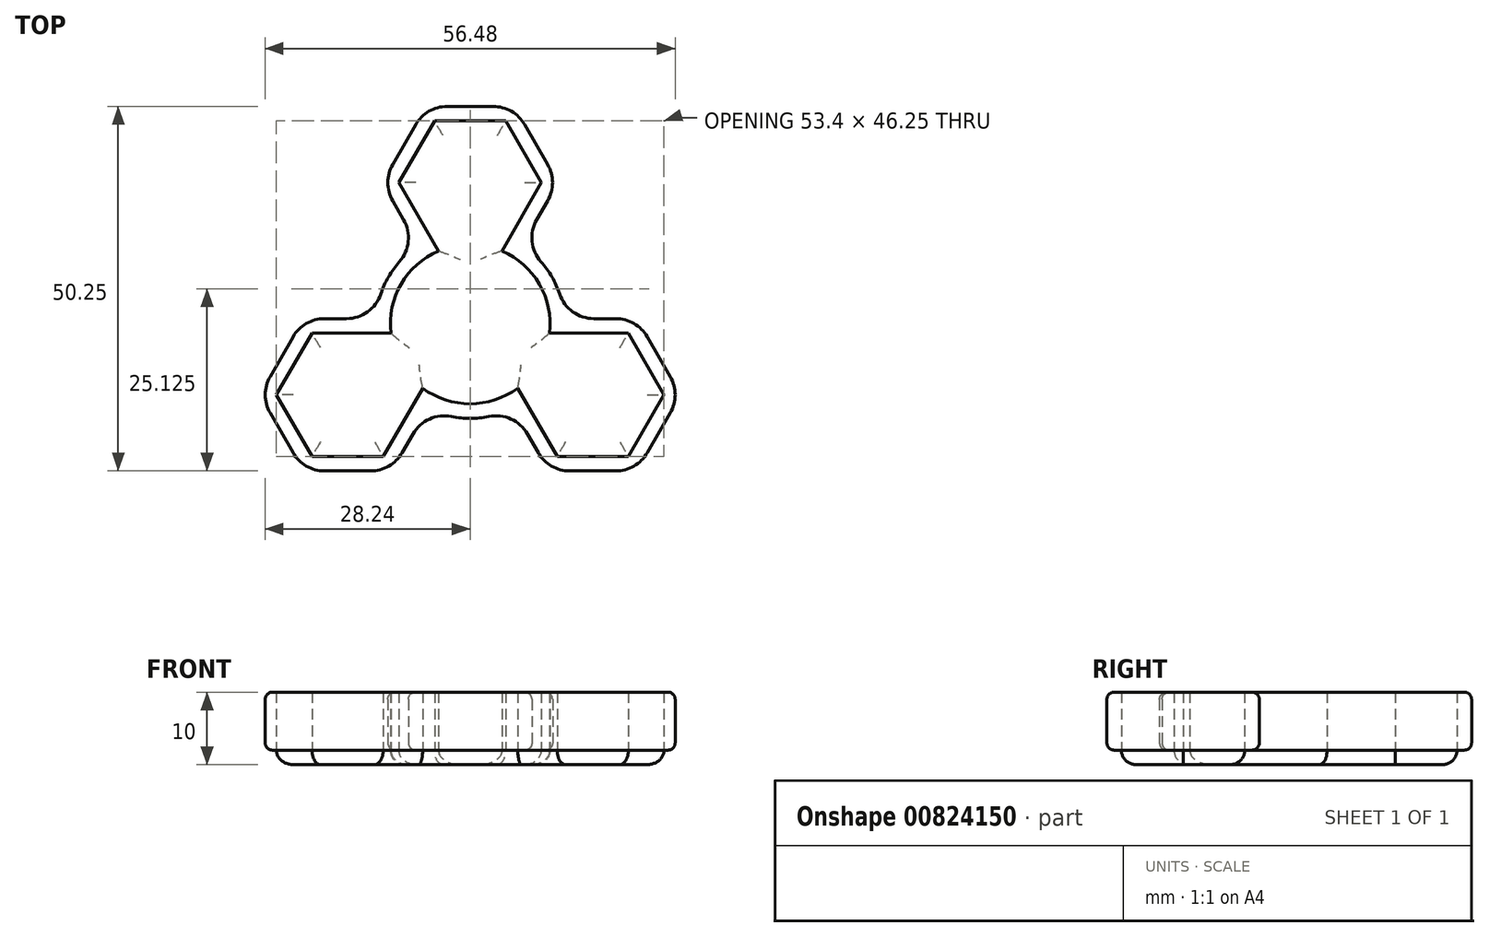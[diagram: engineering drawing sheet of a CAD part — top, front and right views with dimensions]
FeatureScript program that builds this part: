
annotation { "Feature Type Name" : "Feature", "Feature Type Description" : "" }
export const myFeature = defineFeature(function(context is Context, id is Id, definition is map)
    precondition{}
    {
        {
            var Q0;
            Q0=qCreatedBy(makeId("Top.planeOp"),FACE);
            var sketch = newSketch(context, id + "F0", { "sketchPlane" : qUnion([Q0])});
            skCircle(sketch, "E0", {"center": v(0, 0) * mm, "radius": 11 * mm, "construction": true});
            skCircle(sketch, "E1", {"center": v(0, 19.5) * mm, "radius": 8.5 * mm, "construction": true});
            skLineSegment(sketch, "E2", {"start": v(0, 19.5) * mm, "end": v(0, 0) * mm, "construction": true});
            skLineSegment(sketch, "E3", {"start": v(-4.9, 28) * mm, "end": v(4.9, 28) * mm});
            skLineSegment(sketch, "E4", {"start": v(-4.9, 28) * mm, "end": v(-9.81, 19.5) * mm});
            skLineSegment(sketch, "E5", {"start": v(-9.81, 19.5) * mm, "end": v(-4.9, 11) * mm});
            skLineSegment(sketch, "E6", {"start": v(-4.9, 11) * mm, "end": v(4.9, 11) * mm, "construction": true});
            skLineSegment(sketch, "E7", {"start": v(4.9, 11) * mm, "end": v(9.81, 19.5) * mm});
            skLineSegment(sketch, "E8", {"start": v(9.81, 19.5) * mm, "end": v(4.9, 28) * mm});
            skCircle(sketch, "E9", {"center": v(16.89, -9.75) * mm, "radius": 8.5 * mm, "construction": true});
            skLineSegment(sketch, "E10", {"start": v(11.98, -1.25) * mm, "end": v(21.8, -1.25) * mm});
            skLineSegment(sketch, "E11", {"start": v(11.98, -1.25) * mm, "end": v(7.07, -9.75) * mm, "construction": true});
            skLineSegment(sketch, "E12", {"start": v(7.07, -9.75) * mm, "end": v(11.98, -18.25) * mm});
            skLineSegment(sketch, "E13", {"start": v(11.98, -18.25) * mm, "end": v(21.8, -18.25) * mm});
            skLineSegment(sketch, "E14", {"start": v(21.8, -18.25) * mm, "end": v(26.7, -9.75) * mm});
            skLineSegment(sketch, "E15", {"start": v(26.7, -9.75) * mm, "end": v(21.8, -1.25) * mm});
            skLineSegment(sketch, "E16", {"start": v(0, 0) * mm, "end": v(16.89, -9.75) * mm, "construction": true});
            skCircle(sketch, "E17", {"center": v(-16.89, -9.75) * mm, "radius": 8.5 * mm, "construction": true});
            skLineSegment(sketch, "E18", {"start": v(-21.8, -1.25) * mm, "end": v(-11.98, -1.25) * mm});
            skLineSegment(sketch, "E19", {"start": v(-21.8, -1.25) * mm, "end": v(-26.7, -9.75) * mm});
            skLineSegment(sketch, "E20", {"start": v(-26.7, -9.75) * mm, "end": v(-21.8, -18.25) * mm});
            skLineSegment(sketch, "E21", {"start": v(-21.8, -18.25) * mm, "end": v(-11.98, -18.25) * mm});
            skLineSegment(sketch, "E22", {"start": v(-11.98, -18.25) * mm, "end": v(-7.07, -9.75) * mm});
            skLineSegment(sketch, "E23", {"start": v(-7.07, -9.75) * mm, "end": v(-11.98, -1.25) * mm, "construction": true});
            skLineSegment(sketch, "E24", {"start": v(-16.89, -9.75) * mm, "end": v(0, 0) * mm, "construction": true});
            skLineSegment(sketch, "E25", {"start": v(-4.9, 11) * mm, "end": v(-4.38, 10.09) * mm});
            skLineSegment(sketch, "E26", {"start": v(4.9, 11) * mm, "end": v(4.38, 10.09) * mm});
            skLineSegment(sketch, "E27", {"start": v(-11.98, -1.25) * mm, "end": v(-10.93, -1.25) * mm});
            skLineSegment(sketch, "E28", {"start": v(-7.07, -9.75) * mm, "end": v(-6.55, -8.84) * mm});
            skLineSegment(sketch, "E29", {"start": v(7.07, -9.75) * mm, "end": v(6.55, -8.84) * mm});
            skLineSegment(sketch, "E30", {"start": v(11.98, -1.25) * mm, "end": v(10.93, -1.25) * mm});
            skArc(sketch, "E31", {"start": v(-4.38, 10.09) * mm, "mid": v(-9.53, 5.5) * mm, "end": v(-10.93, -1.25) * mm});
            skArc(sketch, "E32", {"start": v(4.38, 10.09) * mm, "mid": v(9.53, 5.5) * mm, "end": v(10.93, -1.25) * mm});
            skArc(sketch, "E33", {"start": v(-6.55, -8.84) * mm, "mid": v(0, -11) * mm, "end": v(6.55, -8.84) * mm});
            skLineSegment(sketch, "E34.0", {"start": v(-6.06, 30) * mm, "end": v(-12.12, 19.5) * mm});
            skLineSegment(sketch, "E34.1", {"start": v(-6.06, 30) * mm, "end": v(6.06, 30) * mm});
            skLineSegment(sketch, "E34.2", {"start": v(12.12, 19.5) * mm, "end": v(6.06, 30) * mm});
            skLineSegment(sketch, "E34.3", {"start": v(7.14, 10.86) * mm, "end": v(12.12, 19.5) * mm});
            skArc(sketch, "E34.4", {"start": v(7.14, 10.86) * mm, "mid": v(11.26, 6.5) * mm, "end": v(12.98, 0.75) * mm});
            skLineSegment(sketch, "E34.5", {"start": v(-12.12, 19.5) * mm, "end": v(-7.14, 10.86) * mm});
            skLineSegment(sketch, "E34.6", {"start": v(12.98, 0.75) * mm, "end": v(22.95, 0.75) * mm});
            skLineSegment(sketch, "E34.7", {"start": v(29.01, -9.75) * mm, "end": v(22.95, 0.75) * mm});
            skLineSegment(sketch, "E34.8", {"start": v(-29.01, -9.75) * mm, "end": v(-22.95, -20.25) * mm});
            skLineSegment(sketch, "E34.9", {"start": v(-22.95, 0.75) * mm, "end": v(-29.01, -9.75) * mm});
            skLineSegment(sketch, "E34.10", {"start": v(-22.95, 0.75) * mm, "end": v(-12.98, 0.75) * mm});
            skArc(sketch, "E34.11", {"start": v(-7.14, 10.86) * mm, "mid": v(-11.26, 6.5) * mm, "end": v(-12.98, 0.75) * mm});
            skLineSegment(sketch, "E34.12", {"start": v(-22.95, -20.25) * mm, "end": v(-10.83, -20.25) * mm});
            skLineSegment(sketch, "E34.13", {"start": v(-10.83, -20.25) * mm, "end": v(-5.84, -11.61) * mm});
            skArc(sketch, "E34.14", {"start": v(-5.84, -11.61) * mm, "mid": v(0, -13) * mm, "end": v(5.84, -11.61) * mm});
            skLineSegment(sketch, "E34.15", {"start": v(5.84, -11.61) * mm, "end": v(10.83, -20.25) * mm});
            skLineSegment(sketch, "E34.16", {"start": v(10.83, -20.25) * mm, "end": v(22.95, -20.25) * mm});
            skLineSegment(sketch, "E34.17", {"start": v(22.95, -20.25) * mm, "end": v(29.01, -9.75) * mm});
            skSolve(sketch);
        }
        {
            var Q0;
            Q0=makeQuery(id+"F0.imprint","IMPRINT",FACE,{"disambiguationData":[TD([[makeQuery(id+"F0.imprint","IMPRINT",EDGE,{"derivedFrom":sQuery(id+"F0.wireOp",EDGE,"E3")}),1.0]])]});
            extrude(context, id + "F1", {"entities" : qUnion([Q0]), "depth" : 8 * mm, "offsetDistance" : 25 * mm});
        }
        {
            var Q0;
            Q0=makeQuery(id+"F1.opExtrude","SWEPT_EDGE",EDGE,{"disambiguationData":[OSD([sQuery(id+"F0.wireOp",EDGE,"E34.4"),sQuery(id+"F0.wireOp",EDGE,"E34.6")])]});
            var Q1;
            Q1=makeQuery(id+"F1.opExtrude","SWEPT_EDGE",EDGE,{"disambiguationData":[OSD([sQuery(id+"F0.wireOp",EDGE,"E34.3"),sQuery(id+"F0.wireOp",EDGE,"E34.4")])]});
            var Q2;
            Q2=makeQuery(id+"F1.opExtrude","SWEPT_EDGE",EDGE,{"disambiguationData":[OSD([sQuery(id+"F0.wireOp",EDGE,"E34.14"),sQuery(id+"F0.wireOp",EDGE,"E34.15")])]});
            var Q3;
            Q3=makeQuery(id+"F1.opExtrude","SWEPT_EDGE",EDGE,{"disambiguationData":[OSD([sQuery(id+"F0.wireOp",EDGE,"E34.13"),sQuery(id+"F0.wireOp",EDGE,"E34.14")])]});
            var Q4;
            Q4=makeQuery(id+"F1.opExtrude","SWEPT_EDGE",EDGE,{"disambiguationData":[OSD([sQuery(id+"F0.wireOp",EDGE,"E34.10"),sQuery(id+"F0.wireOp",EDGE,"E34.11")])]});
            var Q5;
            Q5=makeQuery(id+"F1.opExtrude","SWEPT_EDGE",EDGE,{"disambiguationData":[OSD([sQuery(id+"F0.wireOp",EDGE,"E34.5"),sQuery(id+"F0.wireOp",EDGE,"E34.11")])]});
            fillet(context, id + "F2", {"entities" : qUnion([Q0, Q1, Q2, Q3, Q4, Q5]), "radius" : 5 * mm, "tangentPropagation" : true, "allowEdgeOverflow" : false});
        }
        {
            var Q0;
            Q0=makeQuery(id+"F1.opExtrude","SWEPT_EDGE",EDGE,{"disambiguationData":[OSD([sQuery(id+"F0.wireOp",EDGE,"E34.15"),sQuery(id+"F0.wireOp",EDGE,"E34.16")])]});
            var Q1;
            Q1=makeQuery(id+"F1.opExtrude","SWEPT_EDGE",EDGE,{"disambiguationData":[OSD([sQuery(id+"F0.wireOp",EDGE,"E34.16"),sQuery(id+"F0.wireOp",EDGE,"E34.17")])]});
            var Q2;
            Q2=makeQuery(id+"F1.opExtrude","SWEPT_EDGE",EDGE,{"disambiguationData":[OSD([sQuery(id+"F0.wireOp",EDGE,"E34.7"),sQuery(id+"F0.wireOp",EDGE,"E34.17")])]});
            var Q3;
            Q3=makeQuery(id+"F1.opExtrude","SWEPT_EDGE",EDGE,{"disambiguationData":[OSD([sQuery(id+"F0.wireOp",EDGE,"E34.6"),sQuery(id+"F0.wireOp",EDGE,"E34.7")])]});
            var Q4;
            Q4=makeQuery(id+"F1.opExtrude","SWEPT_EDGE",EDGE,{"disambiguationData":[OSD([sQuery(id+"F0.wireOp",EDGE,"E34.2"),sQuery(id+"F0.wireOp",EDGE,"E34.3")])]});
            var Q5;
            Q5=makeQuery(id+"F1.opExtrude","SWEPT_EDGE",EDGE,{"disambiguationData":[OSD([sQuery(id+"F0.wireOp",EDGE,"E34.1"),sQuery(id+"F0.wireOp",EDGE,"E34.2")])]});
            var Q6;
            Q6=makeQuery(id+"F1.opExtrude","SWEPT_EDGE",EDGE,{"disambiguationData":[OSD([sQuery(id+"F0.wireOp",EDGE,"E34.0"),sQuery(id+"F0.wireOp",EDGE,"E34.1")])]});
            var Q7;
            Q7=makeQuery(id+"F1.opExtrude","SWEPT_EDGE",EDGE,{"disambiguationData":[OSD([sQuery(id+"F0.wireOp",EDGE,"E34.0"),sQuery(id+"F0.wireOp",EDGE,"E34.5")])]});
            var Q8;
            Q8=makeQuery(id+"F1.opExtrude","SWEPT_EDGE",EDGE,{"disambiguationData":[OSD([sQuery(id+"F0.wireOp",EDGE,"E34.9"),sQuery(id+"F0.wireOp",EDGE,"E34.10")])]});
            var Q9;
            Q9=makeQuery(id+"F1.opExtrude","SWEPT_EDGE",EDGE,{"disambiguationData":[OSD([sQuery(id+"F0.wireOp",EDGE,"E34.8"),sQuery(id+"F0.wireOp",EDGE,"E34.9")])]});
            var Q10;
            Q10=makeQuery(id+"F1.opExtrude","SWEPT_EDGE",EDGE,{"disambiguationData":[OSD([sQuery(id+"F0.wireOp",EDGE,"E34.8"),sQuery(id+"F0.wireOp",EDGE,"E34.12")])]});
            var Q11;
            Q11=makeQuery(id+"F1.opExtrude","SWEPT_EDGE",EDGE,{"disambiguationData":[OSD([sQuery(id+"F0.wireOp",EDGE,"E34.12"),sQuery(id+"F0.wireOp",EDGE,"E34.13")])]});
            fillet(context, id + "F3", {"entities" : qUnion([Q0, Q1, Q2, Q3, Q4, Q5, Q6, Q7, Q8, Q9, Q10, Q11]), "radius" : 5 * mm, "tangentPropagation" : true, "allowEdgeOverflow" : false});
        }
        {
            var Q0;
            Q0=makeQuery(id+"F1.opExtrude","CAP_EDGE",EDGE,{"disambiguationData":[OSD([sQuery(id+"F0.wireOp",EDGE,"E34.17")])],"isStart":false});
            var Q1;
            {var subQ0=sQuery(id+"F0.wireOp",EDGE,"E34.17");var subQ1=sQuery(id+"F0.wireOp",EDGE,"E34.16");Q1=makeQuery(id+"F3.opFillet","BLEND_EDGE",EDGE,{"blendedFrom":[makeQuery(id+"F1.opExtrude","SWEPT_EDGE",EDGE,{"disambiguationData":[OSD([subQ1,subQ0])]}),makeQuery(id+"F1.opExtrude","CAP_FACE",FACE,{"disambiguationData":[OSD([sQuery(id+"F0.wireOp",EDGE,"E3"),sQuery(id+"F0.wireOp",EDGE,"E4"),sQuery(id+"F0.wireOp",EDGE,"E5"),sQuery(id+"F0.wireOp",EDGE,"E7"),sQuery(id+"F0.wireOp",EDGE,"E8"),sQuery(id+"F0.wireOp",EDGE,"E10"),sQuery(id+"F0.wireOp",EDGE,"E12"),sQuery(id+"F0.wireOp",EDGE,"E13"),sQuery(id+"F0.wireOp",EDGE,"E14"),sQuery(id+"F0.wireOp",EDGE,"E15"),sQuery(id+"F0.wireOp",EDGE,"E18"),sQuery(id+"F0.wireOp",EDGE,"E19"),sQuery(id+"F0.wireOp",EDGE,"E20"),sQuery(id+"F0.wireOp",EDGE,"E21"),sQuery(id+"F0.wireOp",EDGE,"E22"),sQuery(id+"F0.wireOp",EDGE,"E25"),sQuery(id+"F0.wireOp",EDGE,"E26"),sQuery(id+"F0.wireOp",EDGE,"E27"),sQuery(id+"F0.wireOp",EDGE,"E28"),sQuery(id+"F0.wireOp",EDGE,"E29"),sQuery(id+"F0.wireOp",EDGE,"E30"),sQuery(id+"F0.wireOp",EDGE,"E31"),sQuery(id+"F0.wireOp",EDGE,"E32"),sQuery(id+"F0.wireOp",EDGE,"E33"),sQuery(id+"F0.wireOp",EDGE,"E34.0"),sQuery(id+"F0.wireOp",EDGE,"E34.1"),sQuery(id+"F0.wireOp",EDGE,"E34.2"),sQuery(id+"F0.wireOp",EDGE,"E34.3"),sQuery(id+"F0.wireOp",EDGE,"E34.4"),sQuery(id+"F0.wireOp",EDGE,"E34.5"),sQuery(id+"F0.wireOp",EDGE,"E34.6"),sQuery(id+"F0.wireOp",EDGE,"E34.7"),sQuery(id+"F0.wireOp",EDGE,"E34.8"),sQuery(id+"F0.wireOp",EDGE,"E34.9"),sQuery(id+"F0.wireOp",EDGE,"E34.10"),sQuery(id+"F0.wireOp",EDGE,"E34.11"),sQuery(id+"F0.wireOp",EDGE,"E34.12"),sQuery(id+"F0.wireOp",EDGE,"E34.13"),sQuery(id+"F0.wireOp",EDGE,"E34.14"),sQuery(id+"F0.wireOp",EDGE,"E34.15"),subQ1,subQ0])],"isStart":false})],"blendedInto":[makeQuery(id+"F1.opExtrude","CAP_FACE",FACE,{"disambiguationData":[OSD([sQuery(id+"F0.wireOp",EDGE,"E3"),sQuery(id+"F0.wireOp",EDGE,"E4"),sQuery(id+"F0.wireOp",EDGE,"E5"),sQuery(id+"F0.wireOp",EDGE,"E7"),sQuery(id+"F0.wireOp",EDGE,"E8"),sQuery(id+"F0.wireOp",EDGE,"E10"),sQuery(id+"F0.wireOp",EDGE,"E12"),sQuery(id+"F0.wireOp",EDGE,"E13"),sQuery(id+"F0.wireOp",EDGE,"E14"),sQuery(id+"F0.wireOp",EDGE,"E15"),sQuery(id+"F0.wireOp",EDGE,"E18"),sQuery(id+"F0.wireOp",EDGE,"E19"),sQuery(id+"F0.wireOp",EDGE,"E20"),sQuery(id+"F0.wireOp",EDGE,"E21"),sQuery(id+"F0.wireOp",EDGE,"E22"),sQuery(id+"F0.wireOp",EDGE,"E25"),sQuery(id+"F0.wireOp",EDGE,"E26"),sQuery(id+"F0.wireOp",EDGE,"E27"),sQuery(id+"F0.wireOp",EDGE,"E28"),sQuery(id+"F0.wireOp",EDGE,"E29"),sQuery(id+"F0.wireOp",EDGE,"E30"),sQuery(id+"F0.wireOp",EDGE,"E31"),sQuery(id+"F0.wireOp",EDGE,"E32"),sQuery(id+"F0.wireOp",EDGE,"E33"),sQuery(id+"F0.wireOp",EDGE,"E34.0"),sQuery(id+"F0.wireOp",EDGE,"E34.1"),sQuery(id+"F0.wireOp",EDGE,"E34.2"),sQuery(id+"F0.wireOp",EDGE,"E34.3"),sQuery(id+"F0.wireOp",EDGE,"E34.4"),sQuery(id+"F0.wireOp",EDGE,"E34.5"),sQuery(id+"F0.wireOp",EDGE,"E34.6"),sQuery(id+"F0.wireOp",EDGE,"E34.7"),sQuery(id+"F0.wireOp",EDGE,"E34.8"),sQuery(id+"F0.wireOp",EDGE,"E34.9"),sQuery(id+"F0.wireOp",EDGE,"E34.10"),sQuery(id+"F0.wireOp",EDGE,"E34.11"),sQuery(id+"F0.wireOp",EDGE,"E34.12"),sQuery(id+"F0.wireOp",EDGE,"E34.13"),sQuery(id+"F0.wireOp",EDGE,"E34.14"),sQuery(id+"F0.wireOp",EDGE,"E34.15"),subQ1,subQ0])],"isStart":false})]});}
            var Q2;
            Q2=makeQuery(id+"F1.opExtrude","CAP_EDGE",EDGE,{"disambiguationData":[OSD([sQuery(id+"F0.wireOp",EDGE,"E34.16")])],"isStart":false});
            var Q3;
            {var subQ0=sQuery(id+"F0.wireOp",EDGE,"E34.16");var subQ1=sQuery(id+"F0.wireOp",EDGE,"E34.15");Q3=makeQuery(id+"F3.opFillet","BLEND_EDGE",EDGE,{"blendedFrom":[makeQuery(id+"F1.opExtrude","SWEPT_EDGE",EDGE,{"disambiguationData":[OSD([subQ1,subQ0])]}),makeQuery(id+"F1.opExtrude","CAP_FACE",FACE,{"disambiguationData":[OSD([sQuery(id+"F0.wireOp",EDGE,"E3"),sQuery(id+"F0.wireOp",EDGE,"E4"),sQuery(id+"F0.wireOp",EDGE,"E5"),sQuery(id+"F0.wireOp",EDGE,"E7"),sQuery(id+"F0.wireOp",EDGE,"E8"),sQuery(id+"F0.wireOp",EDGE,"E10"),sQuery(id+"F0.wireOp",EDGE,"E12"),sQuery(id+"F0.wireOp",EDGE,"E13"),sQuery(id+"F0.wireOp",EDGE,"E14"),sQuery(id+"F0.wireOp",EDGE,"E15"),sQuery(id+"F0.wireOp",EDGE,"E18"),sQuery(id+"F0.wireOp",EDGE,"E19"),sQuery(id+"F0.wireOp",EDGE,"E20"),sQuery(id+"F0.wireOp",EDGE,"E21"),sQuery(id+"F0.wireOp",EDGE,"E22"),sQuery(id+"F0.wireOp",EDGE,"E25"),sQuery(id+"F0.wireOp",EDGE,"E26"),sQuery(id+"F0.wireOp",EDGE,"E27"),sQuery(id+"F0.wireOp",EDGE,"E28"),sQuery(id+"F0.wireOp",EDGE,"E29"),sQuery(id+"F0.wireOp",EDGE,"E30"),sQuery(id+"F0.wireOp",EDGE,"E31"),sQuery(id+"F0.wireOp",EDGE,"E32"),sQuery(id+"F0.wireOp",EDGE,"E33"),sQuery(id+"F0.wireOp",EDGE,"E34.0"),sQuery(id+"F0.wireOp",EDGE,"E34.1"),sQuery(id+"F0.wireOp",EDGE,"E34.2"),sQuery(id+"F0.wireOp",EDGE,"E34.3"),sQuery(id+"F0.wireOp",EDGE,"E34.4"),sQuery(id+"F0.wireOp",EDGE,"E34.5"),sQuery(id+"F0.wireOp",EDGE,"E34.6"),sQuery(id+"F0.wireOp",EDGE,"E34.7"),sQuery(id+"F0.wireOp",EDGE,"E34.8"),sQuery(id+"F0.wireOp",EDGE,"E34.9"),sQuery(id+"F0.wireOp",EDGE,"E34.10"),sQuery(id+"F0.wireOp",EDGE,"E34.11"),sQuery(id+"F0.wireOp",EDGE,"E34.12"),sQuery(id+"F0.wireOp",EDGE,"E34.13"),sQuery(id+"F0.wireOp",EDGE,"E34.14"),subQ1,subQ0,sQuery(id+"F0.wireOp",EDGE,"E34.17")])],"isStart":false})],"blendedInto":[makeQuery(id+"F1.opExtrude","CAP_FACE",FACE,{"disambiguationData":[OSD([sQuery(id+"F0.wireOp",EDGE,"E3"),sQuery(id+"F0.wireOp",EDGE,"E4"),sQuery(id+"F0.wireOp",EDGE,"E5"),sQuery(id+"F0.wireOp",EDGE,"E7"),sQuery(id+"F0.wireOp",EDGE,"E8"),sQuery(id+"F0.wireOp",EDGE,"E10"),sQuery(id+"F0.wireOp",EDGE,"E12"),sQuery(id+"F0.wireOp",EDGE,"E13"),sQuery(id+"F0.wireOp",EDGE,"E14"),sQuery(id+"F0.wireOp",EDGE,"E15"),sQuery(id+"F0.wireOp",EDGE,"E18"),sQuery(id+"F0.wireOp",EDGE,"E19"),sQuery(id+"F0.wireOp",EDGE,"E20"),sQuery(id+"F0.wireOp",EDGE,"E21"),sQuery(id+"F0.wireOp",EDGE,"E22"),sQuery(id+"F0.wireOp",EDGE,"E25"),sQuery(id+"F0.wireOp",EDGE,"E26"),sQuery(id+"F0.wireOp",EDGE,"E27"),sQuery(id+"F0.wireOp",EDGE,"E28"),sQuery(id+"F0.wireOp",EDGE,"E29"),sQuery(id+"F0.wireOp",EDGE,"E30"),sQuery(id+"F0.wireOp",EDGE,"E31"),sQuery(id+"F0.wireOp",EDGE,"E32"),sQuery(id+"F0.wireOp",EDGE,"E33"),sQuery(id+"F0.wireOp",EDGE,"E34.0"),sQuery(id+"F0.wireOp",EDGE,"E34.1"),sQuery(id+"F0.wireOp",EDGE,"E34.2"),sQuery(id+"F0.wireOp",EDGE,"E34.3"),sQuery(id+"F0.wireOp",EDGE,"E34.4"),sQuery(id+"F0.wireOp",EDGE,"E34.5"),sQuery(id+"F0.wireOp",EDGE,"E34.6"),sQuery(id+"F0.wireOp",EDGE,"E34.7"),sQuery(id+"F0.wireOp",EDGE,"E34.8"),sQuery(id+"F0.wireOp",EDGE,"E34.9"),sQuery(id+"F0.wireOp",EDGE,"E34.10"),sQuery(id+"F0.wireOp",EDGE,"E34.11"),sQuery(id+"F0.wireOp",EDGE,"E34.12"),sQuery(id+"F0.wireOp",EDGE,"E34.13"),sQuery(id+"F0.wireOp",EDGE,"E34.14"),subQ1,subQ0,sQuery(id+"F0.wireOp",EDGE,"E34.17")])],"isStart":false})]});}
            var Q4;
            Q4=makeQuery(id+"F1.opExtrude","CAP_EDGE",EDGE,{"disambiguationData":[OSD([sQuery(id+"F0.wireOp",EDGE,"E34.15")])],"isStart":false});
            var Q5;
            {var subQ0=sQuery(id+"F0.wireOp",EDGE,"E34.15");var subQ1=sQuery(id+"F0.wireOp",EDGE,"E34.14");Q5=makeQuery(id+"F2.opFillet","BLEND_EDGE",EDGE,{"blendedFrom":[makeQuery(id+"F1.opExtrude","SWEPT_EDGE",EDGE,{"disambiguationData":[OSD([subQ1,subQ0])]}),makeQuery(id+"F1.opExtrude","CAP_FACE",FACE,{"disambiguationData":[OSD([sQuery(id+"F0.wireOp",EDGE,"E3"),sQuery(id+"F0.wireOp",EDGE,"E4"),sQuery(id+"F0.wireOp",EDGE,"E5"),sQuery(id+"F0.wireOp",EDGE,"E7"),sQuery(id+"F0.wireOp",EDGE,"E8"),sQuery(id+"F0.wireOp",EDGE,"E10"),sQuery(id+"F0.wireOp",EDGE,"E12"),sQuery(id+"F0.wireOp",EDGE,"E13"),sQuery(id+"F0.wireOp",EDGE,"E14"),sQuery(id+"F0.wireOp",EDGE,"E15"),sQuery(id+"F0.wireOp",EDGE,"E18"),sQuery(id+"F0.wireOp",EDGE,"E19"),sQuery(id+"F0.wireOp",EDGE,"E20"),sQuery(id+"F0.wireOp",EDGE,"E21"),sQuery(id+"F0.wireOp",EDGE,"E22"),sQuery(id+"F0.wireOp",EDGE,"E25"),sQuery(id+"F0.wireOp",EDGE,"E26"),sQuery(id+"F0.wireOp",EDGE,"E27"),sQuery(id+"F0.wireOp",EDGE,"E28"),sQuery(id+"F0.wireOp",EDGE,"E29"),sQuery(id+"F0.wireOp",EDGE,"E30"),sQuery(id+"F0.wireOp",EDGE,"E31"),sQuery(id+"F0.wireOp",EDGE,"E32"),sQuery(id+"F0.wireOp",EDGE,"E33"),sQuery(id+"F0.wireOp",EDGE,"E34.0"),sQuery(id+"F0.wireOp",EDGE,"E34.1"),sQuery(id+"F0.wireOp",EDGE,"E34.2"),sQuery(id+"F0.wireOp",EDGE,"E34.3"),sQuery(id+"F0.wireOp",EDGE,"E34.4"),sQuery(id+"F0.wireOp",EDGE,"E34.5"),sQuery(id+"F0.wireOp",EDGE,"E34.6"),sQuery(id+"F0.wireOp",EDGE,"E34.7"),sQuery(id+"F0.wireOp",EDGE,"E34.8"),sQuery(id+"F0.wireOp",EDGE,"E34.9"),sQuery(id+"F0.wireOp",EDGE,"E34.10"),sQuery(id+"F0.wireOp",EDGE,"E34.11"),sQuery(id+"F0.wireOp",EDGE,"E34.12"),sQuery(id+"F0.wireOp",EDGE,"E34.13"),subQ1,subQ0,sQuery(id+"F0.wireOp",EDGE,"E34.16"),sQuery(id+"F0.wireOp",EDGE,"E34.17")])],"isStart":false})],"blendedInto":[makeQuery(id+"F1.opExtrude","CAP_FACE",FACE,{"disambiguationData":[OSD([sQuery(id+"F0.wireOp",EDGE,"E3"),sQuery(id+"F0.wireOp",EDGE,"E4"),sQuery(id+"F0.wireOp",EDGE,"E5"),sQuery(id+"F0.wireOp",EDGE,"E7"),sQuery(id+"F0.wireOp",EDGE,"E8"),sQuery(id+"F0.wireOp",EDGE,"E10"),sQuery(id+"F0.wireOp",EDGE,"E12"),sQuery(id+"F0.wireOp",EDGE,"E13"),sQuery(id+"F0.wireOp",EDGE,"E14"),sQuery(id+"F0.wireOp",EDGE,"E15"),sQuery(id+"F0.wireOp",EDGE,"E18"),sQuery(id+"F0.wireOp",EDGE,"E19"),sQuery(id+"F0.wireOp",EDGE,"E20"),sQuery(id+"F0.wireOp",EDGE,"E21"),sQuery(id+"F0.wireOp",EDGE,"E22"),sQuery(id+"F0.wireOp",EDGE,"E25"),sQuery(id+"F0.wireOp",EDGE,"E26"),sQuery(id+"F0.wireOp",EDGE,"E27"),sQuery(id+"F0.wireOp",EDGE,"E28"),sQuery(id+"F0.wireOp",EDGE,"E29"),sQuery(id+"F0.wireOp",EDGE,"E30"),sQuery(id+"F0.wireOp",EDGE,"E31"),sQuery(id+"F0.wireOp",EDGE,"E32"),sQuery(id+"F0.wireOp",EDGE,"E33"),sQuery(id+"F0.wireOp",EDGE,"E34.0"),sQuery(id+"F0.wireOp",EDGE,"E34.1"),sQuery(id+"F0.wireOp",EDGE,"E34.2"),sQuery(id+"F0.wireOp",EDGE,"E34.3"),sQuery(id+"F0.wireOp",EDGE,"E34.4"),sQuery(id+"F0.wireOp",EDGE,"E34.5"),sQuery(id+"F0.wireOp",EDGE,"E34.6"),sQuery(id+"F0.wireOp",EDGE,"E34.7"),sQuery(id+"F0.wireOp",EDGE,"E34.8"),sQuery(id+"F0.wireOp",EDGE,"E34.9"),sQuery(id+"F0.wireOp",EDGE,"E34.10"),sQuery(id+"F0.wireOp",EDGE,"E34.11"),sQuery(id+"F0.wireOp",EDGE,"E34.12"),sQuery(id+"F0.wireOp",EDGE,"E34.13"),subQ1,subQ0,sQuery(id+"F0.wireOp",EDGE,"E34.16"),sQuery(id+"F0.wireOp",EDGE,"E34.17")])],"isStart":false})]});}
            var Q6;
            Q6=makeQuery(id+"F1.opExtrude","CAP_EDGE",EDGE,{"disambiguationData":[OSD([sQuery(id+"F0.wireOp",EDGE,"E34.14")])],"isStart":false});
            var Q7;
            {var subQ0=sQuery(id+"F0.wireOp",EDGE,"E34.14");var subQ1=sQuery(id+"F0.wireOp",EDGE,"E34.13");Q7=makeQuery(id+"F2.opFillet","BLEND_EDGE",EDGE,{"blendedFrom":[makeQuery(id+"F1.opExtrude","SWEPT_EDGE",EDGE,{"disambiguationData":[OSD([subQ1,subQ0])]}),makeQuery(id+"F1.opExtrude","CAP_FACE",FACE,{"disambiguationData":[OSD([sQuery(id+"F0.wireOp",EDGE,"E3"),sQuery(id+"F0.wireOp",EDGE,"E4"),sQuery(id+"F0.wireOp",EDGE,"E5"),sQuery(id+"F0.wireOp",EDGE,"E7"),sQuery(id+"F0.wireOp",EDGE,"E8"),sQuery(id+"F0.wireOp",EDGE,"E10"),sQuery(id+"F0.wireOp",EDGE,"E12"),sQuery(id+"F0.wireOp",EDGE,"E13"),sQuery(id+"F0.wireOp",EDGE,"E14"),sQuery(id+"F0.wireOp",EDGE,"E15"),sQuery(id+"F0.wireOp",EDGE,"E18"),sQuery(id+"F0.wireOp",EDGE,"E19"),sQuery(id+"F0.wireOp",EDGE,"E20"),sQuery(id+"F0.wireOp",EDGE,"E21"),sQuery(id+"F0.wireOp",EDGE,"E22"),sQuery(id+"F0.wireOp",EDGE,"E25"),sQuery(id+"F0.wireOp",EDGE,"E26"),sQuery(id+"F0.wireOp",EDGE,"E27"),sQuery(id+"F0.wireOp",EDGE,"E28"),sQuery(id+"F0.wireOp",EDGE,"E29"),sQuery(id+"F0.wireOp",EDGE,"E30"),sQuery(id+"F0.wireOp",EDGE,"E31"),sQuery(id+"F0.wireOp",EDGE,"E32"),sQuery(id+"F0.wireOp",EDGE,"E33"),sQuery(id+"F0.wireOp",EDGE,"E34.0"),sQuery(id+"F0.wireOp",EDGE,"E34.1"),sQuery(id+"F0.wireOp",EDGE,"E34.2"),sQuery(id+"F0.wireOp",EDGE,"E34.3"),sQuery(id+"F0.wireOp",EDGE,"E34.4"),sQuery(id+"F0.wireOp",EDGE,"E34.5"),sQuery(id+"F0.wireOp",EDGE,"E34.6"),sQuery(id+"F0.wireOp",EDGE,"E34.7"),sQuery(id+"F0.wireOp",EDGE,"E34.8"),sQuery(id+"F0.wireOp",EDGE,"E34.9"),sQuery(id+"F0.wireOp",EDGE,"E34.10"),sQuery(id+"F0.wireOp",EDGE,"E34.11"),sQuery(id+"F0.wireOp",EDGE,"E34.12"),subQ1,subQ0,sQuery(id+"F0.wireOp",EDGE,"E34.15"),sQuery(id+"F0.wireOp",EDGE,"E34.16"),sQuery(id+"F0.wireOp",EDGE,"E34.17")])],"isStart":false})],"blendedInto":[makeQuery(id+"F1.opExtrude","CAP_FACE",FACE,{"disambiguationData":[OSD([sQuery(id+"F0.wireOp",EDGE,"E3"),sQuery(id+"F0.wireOp",EDGE,"E4"),sQuery(id+"F0.wireOp",EDGE,"E5"),sQuery(id+"F0.wireOp",EDGE,"E7"),sQuery(id+"F0.wireOp",EDGE,"E8"),sQuery(id+"F0.wireOp",EDGE,"E10"),sQuery(id+"F0.wireOp",EDGE,"E12"),sQuery(id+"F0.wireOp",EDGE,"E13"),sQuery(id+"F0.wireOp",EDGE,"E14"),sQuery(id+"F0.wireOp",EDGE,"E15"),sQuery(id+"F0.wireOp",EDGE,"E18"),sQuery(id+"F0.wireOp",EDGE,"E19"),sQuery(id+"F0.wireOp",EDGE,"E20"),sQuery(id+"F0.wireOp",EDGE,"E21"),sQuery(id+"F0.wireOp",EDGE,"E22"),sQuery(id+"F0.wireOp",EDGE,"E25"),sQuery(id+"F0.wireOp",EDGE,"E26"),sQuery(id+"F0.wireOp",EDGE,"E27"),sQuery(id+"F0.wireOp",EDGE,"E28"),sQuery(id+"F0.wireOp",EDGE,"E29"),sQuery(id+"F0.wireOp",EDGE,"E30"),sQuery(id+"F0.wireOp",EDGE,"E31"),sQuery(id+"F0.wireOp",EDGE,"E32"),sQuery(id+"F0.wireOp",EDGE,"E33"),sQuery(id+"F0.wireOp",EDGE,"E34.0"),sQuery(id+"F0.wireOp",EDGE,"E34.1"),sQuery(id+"F0.wireOp",EDGE,"E34.2"),sQuery(id+"F0.wireOp",EDGE,"E34.3"),sQuery(id+"F0.wireOp",EDGE,"E34.4"),sQuery(id+"F0.wireOp",EDGE,"E34.5"),sQuery(id+"F0.wireOp",EDGE,"E34.6"),sQuery(id+"F0.wireOp",EDGE,"E34.7"),sQuery(id+"F0.wireOp",EDGE,"E34.8"),sQuery(id+"F0.wireOp",EDGE,"E34.9"),sQuery(id+"F0.wireOp",EDGE,"E34.10"),sQuery(id+"F0.wireOp",EDGE,"E34.11"),sQuery(id+"F0.wireOp",EDGE,"E34.12"),subQ1,subQ0,sQuery(id+"F0.wireOp",EDGE,"E34.15"),sQuery(id+"F0.wireOp",EDGE,"E34.16"),sQuery(id+"F0.wireOp",EDGE,"E34.17")])],"isStart":false})]});}
            var Q8;
            {var subQ0=sQuery(id+"F0.wireOp",EDGE,"E34.13");var subQ1=sQuery(id+"F0.wireOp",EDGE,"E34.12");Q8=makeQuery(id+"F3.opFillet","BLEND_EDGE",EDGE,{"blendedFrom":[makeQuery(id+"F1.opExtrude","SWEPT_EDGE",EDGE,{"disambiguationData":[OSD([subQ1,subQ0])]}),makeQuery(id+"F1.opExtrude","CAP_FACE",FACE,{"disambiguationData":[OSD([sQuery(id+"F0.wireOp",EDGE,"E3"),sQuery(id+"F0.wireOp",EDGE,"E4"),sQuery(id+"F0.wireOp",EDGE,"E5"),sQuery(id+"F0.wireOp",EDGE,"E7"),sQuery(id+"F0.wireOp",EDGE,"E8"),sQuery(id+"F0.wireOp",EDGE,"E10"),sQuery(id+"F0.wireOp",EDGE,"E12"),sQuery(id+"F0.wireOp",EDGE,"E13"),sQuery(id+"F0.wireOp",EDGE,"E14"),sQuery(id+"F0.wireOp",EDGE,"E15"),sQuery(id+"F0.wireOp",EDGE,"E18"),sQuery(id+"F0.wireOp",EDGE,"E19"),sQuery(id+"F0.wireOp",EDGE,"E20"),sQuery(id+"F0.wireOp",EDGE,"E21"),sQuery(id+"F0.wireOp",EDGE,"E22"),sQuery(id+"F0.wireOp",EDGE,"E25"),sQuery(id+"F0.wireOp",EDGE,"E26"),sQuery(id+"F0.wireOp",EDGE,"E27"),sQuery(id+"F0.wireOp",EDGE,"E28"),sQuery(id+"F0.wireOp",EDGE,"E29"),sQuery(id+"F0.wireOp",EDGE,"E30"),sQuery(id+"F0.wireOp",EDGE,"E31"),sQuery(id+"F0.wireOp",EDGE,"E32"),sQuery(id+"F0.wireOp",EDGE,"E33"),sQuery(id+"F0.wireOp",EDGE,"E34.0"),sQuery(id+"F0.wireOp",EDGE,"E34.1"),sQuery(id+"F0.wireOp",EDGE,"E34.2"),sQuery(id+"F0.wireOp",EDGE,"E34.3"),sQuery(id+"F0.wireOp",EDGE,"E34.4"),sQuery(id+"F0.wireOp",EDGE,"E34.5"),sQuery(id+"F0.wireOp",EDGE,"E34.6"),sQuery(id+"F0.wireOp",EDGE,"E34.7"),sQuery(id+"F0.wireOp",EDGE,"E34.8"),sQuery(id+"F0.wireOp",EDGE,"E34.9"),sQuery(id+"F0.wireOp",EDGE,"E34.10"),sQuery(id+"F0.wireOp",EDGE,"E34.11"),subQ1,subQ0,sQuery(id+"F0.wireOp",EDGE,"E34.14"),sQuery(id+"F0.wireOp",EDGE,"E34.15"),sQuery(id+"F0.wireOp",EDGE,"E34.16"),sQuery(id+"F0.wireOp",EDGE,"E34.17")])],"isStart":false})],"blendedInto":[makeQuery(id+"F1.opExtrude","CAP_FACE",FACE,{"disambiguationData":[OSD([sQuery(id+"F0.wireOp",EDGE,"E3"),sQuery(id+"F0.wireOp",EDGE,"E4"),sQuery(id+"F0.wireOp",EDGE,"E5"),sQuery(id+"F0.wireOp",EDGE,"E7"),sQuery(id+"F0.wireOp",EDGE,"E8"),sQuery(id+"F0.wireOp",EDGE,"E10"),sQuery(id+"F0.wireOp",EDGE,"E12"),sQuery(id+"F0.wireOp",EDGE,"E13"),sQuery(id+"F0.wireOp",EDGE,"E14"),sQuery(id+"F0.wireOp",EDGE,"E15"),sQuery(id+"F0.wireOp",EDGE,"E18"),sQuery(id+"F0.wireOp",EDGE,"E19"),sQuery(id+"F0.wireOp",EDGE,"E20"),sQuery(id+"F0.wireOp",EDGE,"E21"),sQuery(id+"F0.wireOp",EDGE,"E22"),sQuery(id+"F0.wireOp",EDGE,"E25"),sQuery(id+"F0.wireOp",EDGE,"E26"),sQuery(id+"F0.wireOp",EDGE,"E27"),sQuery(id+"F0.wireOp",EDGE,"E28"),sQuery(id+"F0.wireOp",EDGE,"E29"),sQuery(id+"F0.wireOp",EDGE,"E30"),sQuery(id+"F0.wireOp",EDGE,"E31"),sQuery(id+"F0.wireOp",EDGE,"E32"),sQuery(id+"F0.wireOp",EDGE,"E33"),sQuery(id+"F0.wireOp",EDGE,"E34.0"),sQuery(id+"F0.wireOp",EDGE,"E34.1"),sQuery(id+"F0.wireOp",EDGE,"E34.2"),sQuery(id+"F0.wireOp",EDGE,"E34.3"),sQuery(id+"F0.wireOp",EDGE,"E34.4"),sQuery(id+"F0.wireOp",EDGE,"E34.5"),sQuery(id+"F0.wireOp",EDGE,"E34.6"),sQuery(id+"F0.wireOp",EDGE,"E34.7"),sQuery(id+"F0.wireOp",EDGE,"E34.8"),sQuery(id+"F0.wireOp",EDGE,"E34.9"),sQuery(id+"F0.wireOp",EDGE,"E34.10"),sQuery(id+"F0.wireOp",EDGE,"E34.11"),subQ1,subQ0,sQuery(id+"F0.wireOp",EDGE,"E34.14"),sQuery(id+"F0.wireOp",EDGE,"E34.15"),sQuery(id+"F0.wireOp",EDGE,"E34.16"),sQuery(id+"F0.wireOp",EDGE,"E34.17")])],"isStart":false})]});}
            var Q9;
            Q9=makeQuery(id+"F1.opExtrude","CAP_EDGE",EDGE,{"disambiguationData":[OSD([sQuery(id+"F0.wireOp",EDGE,"E34.13")])],"isStart":false});
            var Q10;
            Q10=makeQuery(id+"F1.opExtrude","CAP_EDGE",EDGE,{"disambiguationData":[OSD([sQuery(id+"F0.wireOp",EDGE,"E34.12")])],"isStart":false});
            var Q11;
            {var subQ0=sQuery(id+"F0.wireOp",EDGE,"E34.12");var subQ1=sQuery(id+"F0.wireOp",EDGE,"E34.8");Q11=makeQuery(id+"F3.opFillet","BLEND_EDGE",EDGE,{"blendedFrom":[makeQuery(id+"F1.opExtrude","SWEPT_EDGE",EDGE,{"disambiguationData":[OSD([subQ1,subQ0])]}),makeQuery(id+"F1.opExtrude","CAP_FACE",FACE,{"disambiguationData":[OSD([sQuery(id+"F0.wireOp",EDGE,"E3"),sQuery(id+"F0.wireOp",EDGE,"E4"),sQuery(id+"F0.wireOp",EDGE,"E5"),sQuery(id+"F0.wireOp",EDGE,"E7"),sQuery(id+"F0.wireOp",EDGE,"E8"),sQuery(id+"F0.wireOp",EDGE,"E10"),sQuery(id+"F0.wireOp",EDGE,"E12"),sQuery(id+"F0.wireOp",EDGE,"E13"),sQuery(id+"F0.wireOp",EDGE,"E14"),sQuery(id+"F0.wireOp",EDGE,"E15"),sQuery(id+"F0.wireOp",EDGE,"E18"),sQuery(id+"F0.wireOp",EDGE,"E19"),sQuery(id+"F0.wireOp",EDGE,"E20"),sQuery(id+"F0.wireOp",EDGE,"E21"),sQuery(id+"F0.wireOp",EDGE,"E22"),sQuery(id+"F0.wireOp",EDGE,"E25"),sQuery(id+"F0.wireOp",EDGE,"E26"),sQuery(id+"F0.wireOp",EDGE,"E27"),sQuery(id+"F0.wireOp",EDGE,"E28"),sQuery(id+"F0.wireOp",EDGE,"E29"),sQuery(id+"F0.wireOp",EDGE,"E30"),sQuery(id+"F0.wireOp",EDGE,"E31"),sQuery(id+"F0.wireOp",EDGE,"E32"),sQuery(id+"F0.wireOp",EDGE,"E33"),sQuery(id+"F0.wireOp",EDGE,"E34.0"),sQuery(id+"F0.wireOp",EDGE,"E34.1"),sQuery(id+"F0.wireOp",EDGE,"E34.2"),sQuery(id+"F0.wireOp",EDGE,"E34.3"),sQuery(id+"F0.wireOp",EDGE,"E34.4"),sQuery(id+"F0.wireOp",EDGE,"E34.5"),sQuery(id+"F0.wireOp",EDGE,"E34.6"),sQuery(id+"F0.wireOp",EDGE,"E34.7"),subQ1,sQuery(id+"F0.wireOp",EDGE,"E34.9"),sQuery(id+"F0.wireOp",EDGE,"E34.10"),sQuery(id+"F0.wireOp",EDGE,"E34.11"),subQ0,sQuery(id+"F0.wireOp",EDGE,"E34.13"),sQuery(id+"F0.wireOp",EDGE,"E34.14"),sQuery(id+"F0.wireOp",EDGE,"E34.15"),sQuery(id+"F0.wireOp",EDGE,"E34.16"),sQuery(id+"F0.wireOp",EDGE,"E34.17")])],"isStart":false})],"blendedInto":[makeQuery(id+"F1.opExtrude","CAP_FACE",FACE,{"disambiguationData":[OSD([sQuery(id+"F0.wireOp",EDGE,"E3"),sQuery(id+"F0.wireOp",EDGE,"E4"),sQuery(id+"F0.wireOp",EDGE,"E5"),sQuery(id+"F0.wireOp",EDGE,"E7"),sQuery(id+"F0.wireOp",EDGE,"E8"),sQuery(id+"F0.wireOp",EDGE,"E10"),sQuery(id+"F0.wireOp",EDGE,"E12"),sQuery(id+"F0.wireOp",EDGE,"E13"),sQuery(id+"F0.wireOp",EDGE,"E14"),sQuery(id+"F0.wireOp",EDGE,"E15"),sQuery(id+"F0.wireOp",EDGE,"E18"),sQuery(id+"F0.wireOp",EDGE,"E19"),sQuery(id+"F0.wireOp",EDGE,"E20"),sQuery(id+"F0.wireOp",EDGE,"E21"),sQuery(id+"F0.wireOp",EDGE,"E22"),sQuery(id+"F0.wireOp",EDGE,"E25"),sQuery(id+"F0.wireOp",EDGE,"E26"),sQuery(id+"F0.wireOp",EDGE,"E27"),sQuery(id+"F0.wireOp",EDGE,"E28"),sQuery(id+"F0.wireOp",EDGE,"E29"),sQuery(id+"F0.wireOp",EDGE,"E30"),sQuery(id+"F0.wireOp",EDGE,"E31"),sQuery(id+"F0.wireOp",EDGE,"E32"),sQuery(id+"F0.wireOp",EDGE,"E33"),sQuery(id+"F0.wireOp",EDGE,"E34.0"),sQuery(id+"F0.wireOp",EDGE,"E34.1"),sQuery(id+"F0.wireOp",EDGE,"E34.2"),sQuery(id+"F0.wireOp",EDGE,"E34.3"),sQuery(id+"F0.wireOp",EDGE,"E34.4"),sQuery(id+"F0.wireOp",EDGE,"E34.5"),sQuery(id+"F0.wireOp",EDGE,"E34.6"),sQuery(id+"F0.wireOp",EDGE,"E34.7"),subQ1,sQuery(id+"F0.wireOp",EDGE,"E34.9"),sQuery(id+"F0.wireOp",EDGE,"E34.10"),sQuery(id+"F0.wireOp",EDGE,"E34.11"),subQ0,sQuery(id+"F0.wireOp",EDGE,"E34.13"),sQuery(id+"F0.wireOp",EDGE,"E34.14"),sQuery(id+"F0.wireOp",EDGE,"E34.15"),sQuery(id+"F0.wireOp",EDGE,"E34.16"),sQuery(id+"F0.wireOp",EDGE,"E34.17")])],"isStart":false})]});}
            var Q12;
            Q12=makeQuery(id+"F1.opExtrude","CAP_EDGE",EDGE,{"disambiguationData":[OSD([sQuery(id+"F0.wireOp",EDGE,"E34.8")])],"isStart":false});
            var Q13;
            {var subQ0=sQuery(id+"F0.wireOp",EDGE,"E34.9");var subQ1=sQuery(id+"F0.wireOp",EDGE,"E34.8");Q13=makeQuery(id+"F3.opFillet","BLEND_EDGE",EDGE,{"blendedFrom":[makeQuery(id+"F1.opExtrude","SWEPT_EDGE",EDGE,{"disambiguationData":[OSD([subQ1,subQ0])]}),makeQuery(id+"F1.opExtrude","CAP_FACE",FACE,{"disambiguationData":[OSD([sQuery(id+"F0.wireOp",EDGE,"E3"),sQuery(id+"F0.wireOp",EDGE,"E4"),sQuery(id+"F0.wireOp",EDGE,"E5"),sQuery(id+"F0.wireOp",EDGE,"E7"),sQuery(id+"F0.wireOp",EDGE,"E8"),sQuery(id+"F0.wireOp",EDGE,"E10"),sQuery(id+"F0.wireOp",EDGE,"E12"),sQuery(id+"F0.wireOp",EDGE,"E13"),sQuery(id+"F0.wireOp",EDGE,"E14"),sQuery(id+"F0.wireOp",EDGE,"E15"),sQuery(id+"F0.wireOp",EDGE,"E18"),sQuery(id+"F0.wireOp",EDGE,"E19"),sQuery(id+"F0.wireOp",EDGE,"E20"),sQuery(id+"F0.wireOp",EDGE,"E21"),sQuery(id+"F0.wireOp",EDGE,"E22"),sQuery(id+"F0.wireOp",EDGE,"E25"),sQuery(id+"F0.wireOp",EDGE,"E26"),sQuery(id+"F0.wireOp",EDGE,"E27"),sQuery(id+"F0.wireOp",EDGE,"E28"),sQuery(id+"F0.wireOp",EDGE,"E29"),sQuery(id+"F0.wireOp",EDGE,"E30"),sQuery(id+"F0.wireOp",EDGE,"E31"),sQuery(id+"F0.wireOp",EDGE,"E32"),sQuery(id+"F0.wireOp",EDGE,"E33"),sQuery(id+"F0.wireOp",EDGE,"E34.0"),sQuery(id+"F0.wireOp",EDGE,"E34.1"),sQuery(id+"F0.wireOp",EDGE,"E34.2"),sQuery(id+"F0.wireOp",EDGE,"E34.3"),sQuery(id+"F0.wireOp",EDGE,"E34.4"),sQuery(id+"F0.wireOp",EDGE,"E34.5"),sQuery(id+"F0.wireOp",EDGE,"E34.6"),sQuery(id+"F0.wireOp",EDGE,"E34.7"),subQ1,subQ0,sQuery(id+"F0.wireOp",EDGE,"E34.10"),sQuery(id+"F0.wireOp",EDGE,"E34.11"),sQuery(id+"F0.wireOp",EDGE,"E34.12"),sQuery(id+"F0.wireOp",EDGE,"E34.13"),sQuery(id+"F0.wireOp",EDGE,"E34.14"),sQuery(id+"F0.wireOp",EDGE,"E34.15"),sQuery(id+"F0.wireOp",EDGE,"E34.16"),sQuery(id+"F0.wireOp",EDGE,"E34.17")])],"isStart":false})],"blendedInto":[makeQuery(id+"F1.opExtrude","CAP_FACE",FACE,{"disambiguationData":[OSD([sQuery(id+"F0.wireOp",EDGE,"E3"),sQuery(id+"F0.wireOp",EDGE,"E4"),sQuery(id+"F0.wireOp",EDGE,"E5"),sQuery(id+"F0.wireOp",EDGE,"E7"),sQuery(id+"F0.wireOp",EDGE,"E8"),sQuery(id+"F0.wireOp",EDGE,"E10"),sQuery(id+"F0.wireOp",EDGE,"E12"),sQuery(id+"F0.wireOp",EDGE,"E13"),sQuery(id+"F0.wireOp",EDGE,"E14"),sQuery(id+"F0.wireOp",EDGE,"E15"),sQuery(id+"F0.wireOp",EDGE,"E18"),sQuery(id+"F0.wireOp",EDGE,"E19"),sQuery(id+"F0.wireOp",EDGE,"E20"),sQuery(id+"F0.wireOp",EDGE,"E21"),sQuery(id+"F0.wireOp",EDGE,"E22"),sQuery(id+"F0.wireOp",EDGE,"E25"),sQuery(id+"F0.wireOp",EDGE,"E26"),sQuery(id+"F0.wireOp",EDGE,"E27"),sQuery(id+"F0.wireOp",EDGE,"E28"),sQuery(id+"F0.wireOp",EDGE,"E29"),sQuery(id+"F0.wireOp",EDGE,"E30"),sQuery(id+"F0.wireOp",EDGE,"E31"),sQuery(id+"F0.wireOp",EDGE,"E32"),sQuery(id+"F0.wireOp",EDGE,"E33"),sQuery(id+"F0.wireOp",EDGE,"E34.0"),sQuery(id+"F0.wireOp",EDGE,"E34.1"),sQuery(id+"F0.wireOp",EDGE,"E34.2"),sQuery(id+"F0.wireOp",EDGE,"E34.3"),sQuery(id+"F0.wireOp",EDGE,"E34.4"),sQuery(id+"F0.wireOp",EDGE,"E34.5"),sQuery(id+"F0.wireOp",EDGE,"E34.6"),sQuery(id+"F0.wireOp",EDGE,"E34.7"),subQ1,subQ0,sQuery(id+"F0.wireOp",EDGE,"E34.10"),sQuery(id+"F0.wireOp",EDGE,"E34.11"),sQuery(id+"F0.wireOp",EDGE,"E34.12"),sQuery(id+"F0.wireOp",EDGE,"E34.13"),sQuery(id+"F0.wireOp",EDGE,"E34.14"),sQuery(id+"F0.wireOp",EDGE,"E34.15"),sQuery(id+"F0.wireOp",EDGE,"E34.16"),sQuery(id+"F0.wireOp",EDGE,"E34.17")])],"isStart":false})]});}
            var Q14;
            Q14=makeQuery(id+"F1.opExtrude","CAP_EDGE",EDGE,{"disambiguationData":[OSD([sQuery(id+"F0.wireOp",EDGE,"E34.9")])],"isStart":false});
            var Q15;
            {var subQ0=sQuery(id+"F0.wireOp",EDGE,"E34.10");var subQ1=sQuery(id+"F0.wireOp",EDGE,"E34.9");Q15=makeQuery(id+"F3.opFillet","BLEND_EDGE",EDGE,{"blendedFrom":[makeQuery(id+"F1.opExtrude","SWEPT_EDGE",EDGE,{"disambiguationData":[OSD([subQ1,subQ0])]}),makeQuery(id+"F1.opExtrude","CAP_FACE",FACE,{"disambiguationData":[OSD([sQuery(id+"F0.wireOp",EDGE,"E3"),sQuery(id+"F0.wireOp",EDGE,"E4"),sQuery(id+"F0.wireOp",EDGE,"E5"),sQuery(id+"F0.wireOp",EDGE,"E7"),sQuery(id+"F0.wireOp",EDGE,"E8"),sQuery(id+"F0.wireOp",EDGE,"E10"),sQuery(id+"F0.wireOp",EDGE,"E12"),sQuery(id+"F0.wireOp",EDGE,"E13"),sQuery(id+"F0.wireOp",EDGE,"E14"),sQuery(id+"F0.wireOp",EDGE,"E15"),sQuery(id+"F0.wireOp",EDGE,"E18"),sQuery(id+"F0.wireOp",EDGE,"E19"),sQuery(id+"F0.wireOp",EDGE,"E20"),sQuery(id+"F0.wireOp",EDGE,"E21"),sQuery(id+"F0.wireOp",EDGE,"E22"),sQuery(id+"F0.wireOp",EDGE,"E25"),sQuery(id+"F0.wireOp",EDGE,"E26"),sQuery(id+"F0.wireOp",EDGE,"E27"),sQuery(id+"F0.wireOp",EDGE,"E28"),sQuery(id+"F0.wireOp",EDGE,"E29"),sQuery(id+"F0.wireOp",EDGE,"E30"),sQuery(id+"F0.wireOp",EDGE,"E31"),sQuery(id+"F0.wireOp",EDGE,"E32"),sQuery(id+"F0.wireOp",EDGE,"E33"),sQuery(id+"F0.wireOp",EDGE,"E34.0"),sQuery(id+"F0.wireOp",EDGE,"E34.1"),sQuery(id+"F0.wireOp",EDGE,"E34.2"),sQuery(id+"F0.wireOp",EDGE,"E34.3"),sQuery(id+"F0.wireOp",EDGE,"E34.4"),sQuery(id+"F0.wireOp",EDGE,"E34.5"),sQuery(id+"F0.wireOp",EDGE,"E34.6"),sQuery(id+"F0.wireOp",EDGE,"E34.7"),sQuery(id+"F0.wireOp",EDGE,"E34.8"),subQ1,subQ0,sQuery(id+"F0.wireOp",EDGE,"E34.11"),sQuery(id+"F0.wireOp",EDGE,"E34.12"),sQuery(id+"F0.wireOp",EDGE,"E34.13"),sQuery(id+"F0.wireOp",EDGE,"E34.14"),sQuery(id+"F0.wireOp",EDGE,"E34.15"),sQuery(id+"F0.wireOp",EDGE,"E34.16"),sQuery(id+"F0.wireOp",EDGE,"E34.17")])],"isStart":false})],"blendedInto":[makeQuery(id+"F1.opExtrude","CAP_FACE",FACE,{"disambiguationData":[OSD([sQuery(id+"F0.wireOp",EDGE,"E3"),sQuery(id+"F0.wireOp",EDGE,"E4"),sQuery(id+"F0.wireOp",EDGE,"E5"),sQuery(id+"F0.wireOp",EDGE,"E7"),sQuery(id+"F0.wireOp",EDGE,"E8"),sQuery(id+"F0.wireOp",EDGE,"E10"),sQuery(id+"F0.wireOp",EDGE,"E12"),sQuery(id+"F0.wireOp",EDGE,"E13"),sQuery(id+"F0.wireOp",EDGE,"E14"),sQuery(id+"F0.wireOp",EDGE,"E15"),sQuery(id+"F0.wireOp",EDGE,"E18"),sQuery(id+"F0.wireOp",EDGE,"E19"),sQuery(id+"F0.wireOp",EDGE,"E20"),sQuery(id+"F0.wireOp",EDGE,"E21"),sQuery(id+"F0.wireOp",EDGE,"E22"),sQuery(id+"F0.wireOp",EDGE,"E25"),sQuery(id+"F0.wireOp",EDGE,"E26"),sQuery(id+"F0.wireOp",EDGE,"E27"),sQuery(id+"F0.wireOp",EDGE,"E28"),sQuery(id+"F0.wireOp",EDGE,"E29"),sQuery(id+"F0.wireOp",EDGE,"E30"),sQuery(id+"F0.wireOp",EDGE,"E31"),sQuery(id+"F0.wireOp",EDGE,"E32"),sQuery(id+"F0.wireOp",EDGE,"E33"),sQuery(id+"F0.wireOp",EDGE,"E34.0"),sQuery(id+"F0.wireOp",EDGE,"E34.1"),sQuery(id+"F0.wireOp",EDGE,"E34.2"),sQuery(id+"F0.wireOp",EDGE,"E34.3"),sQuery(id+"F0.wireOp",EDGE,"E34.4"),sQuery(id+"F0.wireOp",EDGE,"E34.5"),sQuery(id+"F0.wireOp",EDGE,"E34.6"),sQuery(id+"F0.wireOp",EDGE,"E34.7"),sQuery(id+"F0.wireOp",EDGE,"E34.8"),subQ1,subQ0,sQuery(id+"F0.wireOp",EDGE,"E34.11"),sQuery(id+"F0.wireOp",EDGE,"E34.12"),sQuery(id+"F0.wireOp",EDGE,"E34.13"),sQuery(id+"F0.wireOp",EDGE,"E34.14"),sQuery(id+"F0.wireOp",EDGE,"E34.15"),sQuery(id+"F0.wireOp",EDGE,"E34.16"),sQuery(id+"F0.wireOp",EDGE,"E34.17")])],"isStart":false})]});}
            var Q16;
            Q16=makeQuery(id+"F1.opExtrude","CAP_EDGE",EDGE,{"disambiguationData":[OSD([sQuery(id+"F0.wireOp",EDGE,"E34.10")])],"isStart":false});
            var Q17;
            {var subQ0=sQuery(id+"F0.wireOp",EDGE,"E34.11");var subQ1=sQuery(id+"F0.wireOp",EDGE,"E34.10");Q17=makeQuery(id+"F2.opFillet","BLEND_EDGE",EDGE,{"blendedFrom":[makeQuery(id+"F1.opExtrude","SWEPT_EDGE",EDGE,{"disambiguationData":[OSD([subQ1,subQ0])]}),makeQuery(id+"F1.opExtrude","CAP_FACE",FACE,{"disambiguationData":[OSD([sQuery(id+"F0.wireOp",EDGE,"E3"),sQuery(id+"F0.wireOp",EDGE,"E4"),sQuery(id+"F0.wireOp",EDGE,"E5"),sQuery(id+"F0.wireOp",EDGE,"E7"),sQuery(id+"F0.wireOp",EDGE,"E8"),sQuery(id+"F0.wireOp",EDGE,"E10"),sQuery(id+"F0.wireOp",EDGE,"E12"),sQuery(id+"F0.wireOp",EDGE,"E13"),sQuery(id+"F0.wireOp",EDGE,"E14"),sQuery(id+"F0.wireOp",EDGE,"E15"),sQuery(id+"F0.wireOp",EDGE,"E18"),sQuery(id+"F0.wireOp",EDGE,"E19"),sQuery(id+"F0.wireOp",EDGE,"E20"),sQuery(id+"F0.wireOp",EDGE,"E21"),sQuery(id+"F0.wireOp",EDGE,"E22"),sQuery(id+"F0.wireOp",EDGE,"E25"),sQuery(id+"F0.wireOp",EDGE,"E26"),sQuery(id+"F0.wireOp",EDGE,"E27"),sQuery(id+"F0.wireOp",EDGE,"E28"),sQuery(id+"F0.wireOp",EDGE,"E29"),sQuery(id+"F0.wireOp",EDGE,"E30"),sQuery(id+"F0.wireOp",EDGE,"E31"),sQuery(id+"F0.wireOp",EDGE,"E32"),sQuery(id+"F0.wireOp",EDGE,"E33"),sQuery(id+"F0.wireOp",EDGE,"E34.0"),sQuery(id+"F0.wireOp",EDGE,"E34.1"),sQuery(id+"F0.wireOp",EDGE,"E34.2"),sQuery(id+"F0.wireOp",EDGE,"E34.3"),sQuery(id+"F0.wireOp",EDGE,"E34.4"),sQuery(id+"F0.wireOp",EDGE,"E34.5"),sQuery(id+"F0.wireOp",EDGE,"E34.6"),sQuery(id+"F0.wireOp",EDGE,"E34.7"),sQuery(id+"F0.wireOp",EDGE,"E34.8"),sQuery(id+"F0.wireOp",EDGE,"E34.9"),subQ1,subQ0,sQuery(id+"F0.wireOp",EDGE,"E34.12"),sQuery(id+"F0.wireOp",EDGE,"E34.13"),sQuery(id+"F0.wireOp",EDGE,"E34.14"),sQuery(id+"F0.wireOp",EDGE,"E34.15"),sQuery(id+"F0.wireOp",EDGE,"E34.16"),sQuery(id+"F0.wireOp",EDGE,"E34.17")])],"isStart":false})],"blendedInto":[makeQuery(id+"F1.opExtrude","CAP_FACE",FACE,{"disambiguationData":[OSD([sQuery(id+"F0.wireOp",EDGE,"E3"),sQuery(id+"F0.wireOp",EDGE,"E4"),sQuery(id+"F0.wireOp",EDGE,"E5"),sQuery(id+"F0.wireOp",EDGE,"E7"),sQuery(id+"F0.wireOp",EDGE,"E8"),sQuery(id+"F0.wireOp",EDGE,"E10"),sQuery(id+"F0.wireOp",EDGE,"E12"),sQuery(id+"F0.wireOp",EDGE,"E13"),sQuery(id+"F0.wireOp",EDGE,"E14"),sQuery(id+"F0.wireOp",EDGE,"E15"),sQuery(id+"F0.wireOp",EDGE,"E18"),sQuery(id+"F0.wireOp",EDGE,"E19"),sQuery(id+"F0.wireOp",EDGE,"E20"),sQuery(id+"F0.wireOp",EDGE,"E21"),sQuery(id+"F0.wireOp",EDGE,"E22"),sQuery(id+"F0.wireOp",EDGE,"E25"),sQuery(id+"F0.wireOp",EDGE,"E26"),sQuery(id+"F0.wireOp",EDGE,"E27"),sQuery(id+"F0.wireOp",EDGE,"E28"),sQuery(id+"F0.wireOp",EDGE,"E29"),sQuery(id+"F0.wireOp",EDGE,"E30"),sQuery(id+"F0.wireOp",EDGE,"E31"),sQuery(id+"F0.wireOp",EDGE,"E32"),sQuery(id+"F0.wireOp",EDGE,"E33"),sQuery(id+"F0.wireOp",EDGE,"E34.0"),sQuery(id+"F0.wireOp",EDGE,"E34.1"),sQuery(id+"F0.wireOp",EDGE,"E34.2"),sQuery(id+"F0.wireOp",EDGE,"E34.3"),sQuery(id+"F0.wireOp",EDGE,"E34.4"),sQuery(id+"F0.wireOp",EDGE,"E34.5"),sQuery(id+"F0.wireOp",EDGE,"E34.6"),sQuery(id+"F0.wireOp",EDGE,"E34.7"),sQuery(id+"F0.wireOp",EDGE,"E34.8"),sQuery(id+"F0.wireOp",EDGE,"E34.9"),subQ1,subQ0,sQuery(id+"F0.wireOp",EDGE,"E34.12"),sQuery(id+"F0.wireOp",EDGE,"E34.13"),sQuery(id+"F0.wireOp",EDGE,"E34.14"),sQuery(id+"F0.wireOp",EDGE,"E34.15"),sQuery(id+"F0.wireOp",EDGE,"E34.16"),sQuery(id+"F0.wireOp",EDGE,"E34.17")])],"isStart":false})]});}
            var Q18;
            {var subQ0=sQuery(id+"F0.wireOp",EDGE,"E34.11");var subQ1=sQuery(id+"F0.wireOp",EDGE,"E34.5");Q18=makeQuery(id+"F2.opFillet","BLEND_EDGE",EDGE,{"blendedFrom":[makeQuery(id+"F1.opExtrude","SWEPT_EDGE",EDGE,{"disambiguationData":[OSD([subQ1,subQ0])]}),makeQuery(id+"F1.opExtrude","CAP_FACE",FACE,{"disambiguationData":[OSD([sQuery(id+"F0.wireOp",EDGE,"E3"),sQuery(id+"F0.wireOp",EDGE,"E4"),sQuery(id+"F0.wireOp",EDGE,"E5"),sQuery(id+"F0.wireOp",EDGE,"E7"),sQuery(id+"F0.wireOp",EDGE,"E8"),sQuery(id+"F0.wireOp",EDGE,"E10"),sQuery(id+"F0.wireOp",EDGE,"E12"),sQuery(id+"F0.wireOp",EDGE,"E13"),sQuery(id+"F0.wireOp",EDGE,"E14"),sQuery(id+"F0.wireOp",EDGE,"E15"),sQuery(id+"F0.wireOp",EDGE,"E18"),sQuery(id+"F0.wireOp",EDGE,"E19"),sQuery(id+"F0.wireOp",EDGE,"E20"),sQuery(id+"F0.wireOp",EDGE,"E21"),sQuery(id+"F0.wireOp",EDGE,"E22"),sQuery(id+"F0.wireOp",EDGE,"E25"),sQuery(id+"F0.wireOp",EDGE,"E26"),sQuery(id+"F0.wireOp",EDGE,"E27"),sQuery(id+"F0.wireOp",EDGE,"E28"),sQuery(id+"F0.wireOp",EDGE,"E29"),sQuery(id+"F0.wireOp",EDGE,"E30"),sQuery(id+"F0.wireOp",EDGE,"E31"),sQuery(id+"F0.wireOp",EDGE,"E32"),sQuery(id+"F0.wireOp",EDGE,"E33"),sQuery(id+"F0.wireOp",EDGE,"E34.0"),sQuery(id+"F0.wireOp",EDGE,"E34.1"),sQuery(id+"F0.wireOp",EDGE,"E34.2"),sQuery(id+"F0.wireOp",EDGE,"E34.3"),sQuery(id+"F0.wireOp",EDGE,"E34.4"),subQ1,sQuery(id+"F0.wireOp",EDGE,"E34.6"),sQuery(id+"F0.wireOp",EDGE,"E34.7"),sQuery(id+"F0.wireOp",EDGE,"E34.8"),sQuery(id+"F0.wireOp",EDGE,"E34.9"),sQuery(id+"F0.wireOp",EDGE,"E34.10"),subQ0,sQuery(id+"F0.wireOp",EDGE,"E34.12"),sQuery(id+"F0.wireOp",EDGE,"E34.13"),sQuery(id+"F0.wireOp",EDGE,"E34.14"),sQuery(id+"F0.wireOp",EDGE,"E34.15"),sQuery(id+"F0.wireOp",EDGE,"E34.16"),sQuery(id+"F0.wireOp",EDGE,"E34.17")])],"isStart":false})],"blendedInto":[makeQuery(id+"F1.opExtrude","CAP_FACE",FACE,{"disambiguationData":[OSD([sQuery(id+"F0.wireOp",EDGE,"E3"),sQuery(id+"F0.wireOp",EDGE,"E4"),sQuery(id+"F0.wireOp",EDGE,"E5"),sQuery(id+"F0.wireOp",EDGE,"E7"),sQuery(id+"F0.wireOp",EDGE,"E8"),sQuery(id+"F0.wireOp",EDGE,"E10"),sQuery(id+"F0.wireOp",EDGE,"E12"),sQuery(id+"F0.wireOp",EDGE,"E13"),sQuery(id+"F0.wireOp",EDGE,"E14"),sQuery(id+"F0.wireOp",EDGE,"E15"),sQuery(id+"F0.wireOp",EDGE,"E18"),sQuery(id+"F0.wireOp",EDGE,"E19"),sQuery(id+"F0.wireOp",EDGE,"E20"),sQuery(id+"F0.wireOp",EDGE,"E21"),sQuery(id+"F0.wireOp",EDGE,"E22"),sQuery(id+"F0.wireOp",EDGE,"E25"),sQuery(id+"F0.wireOp",EDGE,"E26"),sQuery(id+"F0.wireOp",EDGE,"E27"),sQuery(id+"F0.wireOp",EDGE,"E28"),sQuery(id+"F0.wireOp",EDGE,"E29"),sQuery(id+"F0.wireOp",EDGE,"E30"),sQuery(id+"F0.wireOp",EDGE,"E31"),sQuery(id+"F0.wireOp",EDGE,"E32"),sQuery(id+"F0.wireOp",EDGE,"E33"),sQuery(id+"F0.wireOp",EDGE,"E34.0"),sQuery(id+"F0.wireOp",EDGE,"E34.1"),sQuery(id+"F0.wireOp",EDGE,"E34.2"),sQuery(id+"F0.wireOp",EDGE,"E34.3"),sQuery(id+"F0.wireOp",EDGE,"E34.4"),subQ1,sQuery(id+"F0.wireOp",EDGE,"E34.6"),sQuery(id+"F0.wireOp",EDGE,"E34.7"),sQuery(id+"F0.wireOp",EDGE,"E34.8"),sQuery(id+"F0.wireOp",EDGE,"E34.9"),sQuery(id+"F0.wireOp",EDGE,"E34.10"),subQ0,sQuery(id+"F0.wireOp",EDGE,"E34.12"),sQuery(id+"F0.wireOp",EDGE,"E34.13"),sQuery(id+"F0.wireOp",EDGE,"E34.14"),sQuery(id+"F0.wireOp",EDGE,"E34.15"),sQuery(id+"F0.wireOp",EDGE,"E34.16"),sQuery(id+"F0.wireOp",EDGE,"E34.17")])],"isStart":false})]});}
            var Q19;
            Q19=makeQuery(id+"F1.opExtrude","CAP_EDGE",EDGE,{"disambiguationData":[OSD([sQuery(id+"F0.wireOp",EDGE,"E34.11")])],"isStart":false});
            var Q20;
            Q20=makeQuery(id+"F1.opExtrude","CAP_EDGE",EDGE,{"disambiguationData":[OSD([sQuery(id+"F0.wireOp",EDGE,"E34.5")])],"isStart":false});
            var Q21;
            {var subQ0=sQuery(id+"F0.wireOp",EDGE,"E34.5");var subQ1=sQuery(id+"F0.wireOp",EDGE,"E34.0");Q21=makeQuery(id+"F3.opFillet","BLEND_EDGE",EDGE,{"blendedFrom":[makeQuery(id+"F1.opExtrude","SWEPT_EDGE",EDGE,{"disambiguationData":[OSD([subQ1,subQ0])]}),makeQuery(id+"F1.opExtrude","CAP_FACE",FACE,{"disambiguationData":[OSD([sQuery(id+"F0.wireOp",EDGE,"E3"),sQuery(id+"F0.wireOp",EDGE,"E4"),sQuery(id+"F0.wireOp",EDGE,"E5"),sQuery(id+"F0.wireOp",EDGE,"E7"),sQuery(id+"F0.wireOp",EDGE,"E8"),sQuery(id+"F0.wireOp",EDGE,"E10"),sQuery(id+"F0.wireOp",EDGE,"E12"),sQuery(id+"F0.wireOp",EDGE,"E13"),sQuery(id+"F0.wireOp",EDGE,"E14"),sQuery(id+"F0.wireOp",EDGE,"E15"),sQuery(id+"F0.wireOp",EDGE,"E18"),sQuery(id+"F0.wireOp",EDGE,"E19"),sQuery(id+"F0.wireOp",EDGE,"E20"),sQuery(id+"F0.wireOp",EDGE,"E21"),sQuery(id+"F0.wireOp",EDGE,"E22"),sQuery(id+"F0.wireOp",EDGE,"E25"),sQuery(id+"F0.wireOp",EDGE,"E26"),sQuery(id+"F0.wireOp",EDGE,"E27"),sQuery(id+"F0.wireOp",EDGE,"E28"),sQuery(id+"F0.wireOp",EDGE,"E29"),sQuery(id+"F0.wireOp",EDGE,"E30"),sQuery(id+"F0.wireOp",EDGE,"E31"),sQuery(id+"F0.wireOp",EDGE,"E32"),sQuery(id+"F0.wireOp",EDGE,"E33"),subQ1,sQuery(id+"F0.wireOp",EDGE,"E34.1"),sQuery(id+"F0.wireOp",EDGE,"E34.2"),sQuery(id+"F0.wireOp",EDGE,"E34.3"),sQuery(id+"F0.wireOp",EDGE,"E34.4"),subQ0,sQuery(id+"F0.wireOp",EDGE,"E34.6"),sQuery(id+"F0.wireOp",EDGE,"E34.7"),sQuery(id+"F0.wireOp",EDGE,"E34.8"),sQuery(id+"F0.wireOp",EDGE,"E34.9"),sQuery(id+"F0.wireOp",EDGE,"E34.10"),sQuery(id+"F0.wireOp",EDGE,"E34.11"),sQuery(id+"F0.wireOp",EDGE,"E34.12"),sQuery(id+"F0.wireOp",EDGE,"E34.13"),sQuery(id+"F0.wireOp",EDGE,"E34.14"),sQuery(id+"F0.wireOp",EDGE,"E34.15"),sQuery(id+"F0.wireOp",EDGE,"E34.16"),sQuery(id+"F0.wireOp",EDGE,"E34.17")])],"isStart":false})],"blendedInto":[makeQuery(id+"F1.opExtrude","CAP_FACE",FACE,{"disambiguationData":[OSD([sQuery(id+"F0.wireOp",EDGE,"E3"),sQuery(id+"F0.wireOp",EDGE,"E4"),sQuery(id+"F0.wireOp",EDGE,"E5"),sQuery(id+"F0.wireOp",EDGE,"E7"),sQuery(id+"F0.wireOp",EDGE,"E8"),sQuery(id+"F0.wireOp",EDGE,"E10"),sQuery(id+"F0.wireOp",EDGE,"E12"),sQuery(id+"F0.wireOp",EDGE,"E13"),sQuery(id+"F0.wireOp",EDGE,"E14"),sQuery(id+"F0.wireOp",EDGE,"E15"),sQuery(id+"F0.wireOp",EDGE,"E18"),sQuery(id+"F0.wireOp",EDGE,"E19"),sQuery(id+"F0.wireOp",EDGE,"E20"),sQuery(id+"F0.wireOp",EDGE,"E21"),sQuery(id+"F0.wireOp",EDGE,"E22"),sQuery(id+"F0.wireOp",EDGE,"E25"),sQuery(id+"F0.wireOp",EDGE,"E26"),sQuery(id+"F0.wireOp",EDGE,"E27"),sQuery(id+"F0.wireOp",EDGE,"E28"),sQuery(id+"F0.wireOp",EDGE,"E29"),sQuery(id+"F0.wireOp",EDGE,"E30"),sQuery(id+"F0.wireOp",EDGE,"E31"),sQuery(id+"F0.wireOp",EDGE,"E32"),sQuery(id+"F0.wireOp",EDGE,"E33"),subQ1,sQuery(id+"F0.wireOp",EDGE,"E34.1"),sQuery(id+"F0.wireOp",EDGE,"E34.2"),sQuery(id+"F0.wireOp",EDGE,"E34.3"),sQuery(id+"F0.wireOp",EDGE,"E34.4"),subQ0,sQuery(id+"F0.wireOp",EDGE,"E34.6"),sQuery(id+"F0.wireOp",EDGE,"E34.7"),sQuery(id+"F0.wireOp",EDGE,"E34.8"),sQuery(id+"F0.wireOp",EDGE,"E34.9"),sQuery(id+"F0.wireOp",EDGE,"E34.10"),sQuery(id+"F0.wireOp",EDGE,"E34.11"),sQuery(id+"F0.wireOp",EDGE,"E34.12"),sQuery(id+"F0.wireOp",EDGE,"E34.13"),sQuery(id+"F0.wireOp",EDGE,"E34.14"),sQuery(id+"F0.wireOp",EDGE,"E34.15"),sQuery(id+"F0.wireOp",EDGE,"E34.16"),sQuery(id+"F0.wireOp",EDGE,"E34.17")])],"isStart":false})]});}
            var Q22;
            Q22=makeQuery(id+"F1.opExtrude","CAP_EDGE",EDGE,{"disambiguationData":[OSD([sQuery(id+"F0.wireOp",EDGE,"E34.0")])],"isStart":false});
            var Q23;
            {var subQ0=sQuery(id+"F0.wireOp",EDGE,"E34.1");var subQ1=sQuery(id+"F0.wireOp",EDGE,"E34.0");Q23=makeQuery(id+"F3.opFillet","BLEND_EDGE",EDGE,{"blendedFrom":[makeQuery(id+"F1.opExtrude","SWEPT_EDGE",EDGE,{"disambiguationData":[OSD([subQ1,subQ0])]}),makeQuery(id+"F1.opExtrude","CAP_FACE",FACE,{"disambiguationData":[OSD([sQuery(id+"F0.wireOp",EDGE,"E3"),sQuery(id+"F0.wireOp",EDGE,"E4"),sQuery(id+"F0.wireOp",EDGE,"E5"),sQuery(id+"F0.wireOp",EDGE,"E7"),sQuery(id+"F0.wireOp",EDGE,"E8"),sQuery(id+"F0.wireOp",EDGE,"E10"),sQuery(id+"F0.wireOp",EDGE,"E12"),sQuery(id+"F0.wireOp",EDGE,"E13"),sQuery(id+"F0.wireOp",EDGE,"E14"),sQuery(id+"F0.wireOp",EDGE,"E15"),sQuery(id+"F0.wireOp",EDGE,"E18"),sQuery(id+"F0.wireOp",EDGE,"E19"),sQuery(id+"F0.wireOp",EDGE,"E20"),sQuery(id+"F0.wireOp",EDGE,"E21"),sQuery(id+"F0.wireOp",EDGE,"E22"),sQuery(id+"F0.wireOp",EDGE,"E25"),sQuery(id+"F0.wireOp",EDGE,"E26"),sQuery(id+"F0.wireOp",EDGE,"E27"),sQuery(id+"F0.wireOp",EDGE,"E28"),sQuery(id+"F0.wireOp",EDGE,"E29"),sQuery(id+"F0.wireOp",EDGE,"E30"),sQuery(id+"F0.wireOp",EDGE,"E31"),sQuery(id+"F0.wireOp",EDGE,"E32"),sQuery(id+"F0.wireOp",EDGE,"E33"),subQ1,subQ0,sQuery(id+"F0.wireOp",EDGE,"E34.2"),sQuery(id+"F0.wireOp",EDGE,"E34.3"),sQuery(id+"F0.wireOp",EDGE,"E34.4"),sQuery(id+"F0.wireOp",EDGE,"E34.5"),sQuery(id+"F0.wireOp",EDGE,"E34.6"),sQuery(id+"F0.wireOp",EDGE,"E34.7"),sQuery(id+"F0.wireOp",EDGE,"E34.8"),sQuery(id+"F0.wireOp",EDGE,"E34.9"),sQuery(id+"F0.wireOp",EDGE,"E34.10"),sQuery(id+"F0.wireOp",EDGE,"E34.11"),sQuery(id+"F0.wireOp",EDGE,"E34.12"),sQuery(id+"F0.wireOp",EDGE,"E34.13"),sQuery(id+"F0.wireOp",EDGE,"E34.14"),sQuery(id+"F0.wireOp",EDGE,"E34.15"),sQuery(id+"F0.wireOp",EDGE,"E34.16"),sQuery(id+"F0.wireOp",EDGE,"E34.17")])],"isStart":false})],"blendedInto":[makeQuery(id+"F1.opExtrude","CAP_FACE",FACE,{"disambiguationData":[OSD([sQuery(id+"F0.wireOp",EDGE,"E3"),sQuery(id+"F0.wireOp",EDGE,"E4"),sQuery(id+"F0.wireOp",EDGE,"E5"),sQuery(id+"F0.wireOp",EDGE,"E7"),sQuery(id+"F0.wireOp",EDGE,"E8"),sQuery(id+"F0.wireOp",EDGE,"E10"),sQuery(id+"F0.wireOp",EDGE,"E12"),sQuery(id+"F0.wireOp",EDGE,"E13"),sQuery(id+"F0.wireOp",EDGE,"E14"),sQuery(id+"F0.wireOp",EDGE,"E15"),sQuery(id+"F0.wireOp",EDGE,"E18"),sQuery(id+"F0.wireOp",EDGE,"E19"),sQuery(id+"F0.wireOp",EDGE,"E20"),sQuery(id+"F0.wireOp",EDGE,"E21"),sQuery(id+"F0.wireOp",EDGE,"E22"),sQuery(id+"F0.wireOp",EDGE,"E25"),sQuery(id+"F0.wireOp",EDGE,"E26"),sQuery(id+"F0.wireOp",EDGE,"E27"),sQuery(id+"F0.wireOp",EDGE,"E28"),sQuery(id+"F0.wireOp",EDGE,"E29"),sQuery(id+"F0.wireOp",EDGE,"E30"),sQuery(id+"F0.wireOp",EDGE,"E31"),sQuery(id+"F0.wireOp",EDGE,"E32"),sQuery(id+"F0.wireOp",EDGE,"E33"),subQ1,subQ0,sQuery(id+"F0.wireOp",EDGE,"E34.2"),sQuery(id+"F0.wireOp",EDGE,"E34.3"),sQuery(id+"F0.wireOp",EDGE,"E34.4"),sQuery(id+"F0.wireOp",EDGE,"E34.5"),sQuery(id+"F0.wireOp",EDGE,"E34.6"),sQuery(id+"F0.wireOp",EDGE,"E34.7"),sQuery(id+"F0.wireOp",EDGE,"E34.8"),sQuery(id+"F0.wireOp",EDGE,"E34.9"),sQuery(id+"F0.wireOp",EDGE,"E34.10"),sQuery(id+"F0.wireOp",EDGE,"E34.11"),sQuery(id+"F0.wireOp",EDGE,"E34.12"),sQuery(id+"F0.wireOp",EDGE,"E34.13"),sQuery(id+"F0.wireOp",EDGE,"E34.14"),sQuery(id+"F0.wireOp",EDGE,"E34.15"),sQuery(id+"F0.wireOp",EDGE,"E34.16"),sQuery(id+"F0.wireOp",EDGE,"E34.17")])],"isStart":false})]});}
            var Q24;
            Q24=makeQuery(id+"F1.opExtrude","CAP_EDGE",EDGE,{"disambiguationData":[OSD([sQuery(id+"F0.wireOp",EDGE,"E34.1")])],"isStart":false});
            var Q25;
            {var subQ0=sQuery(id+"F0.wireOp",EDGE,"E34.2");var subQ1=sQuery(id+"F0.wireOp",EDGE,"E34.1");Q25=makeQuery(id+"F3.opFillet","BLEND_EDGE",EDGE,{"blendedFrom":[makeQuery(id+"F1.opExtrude","SWEPT_EDGE",EDGE,{"disambiguationData":[OSD([subQ1,subQ0])]}),makeQuery(id+"F1.opExtrude","CAP_FACE",FACE,{"disambiguationData":[OSD([sQuery(id+"F0.wireOp",EDGE,"E3"),sQuery(id+"F0.wireOp",EDGE,"E4"),sQuery(id+"F0.wireOp",EDGE,"E5"),sQuery(id+"F0.wireOp",EDGE,"E7"),sQuery(id+"F0.wireOp",EDGE,"E8"),sQuery(id+"F0.wireOp",EDGE,"E10"),sQuery(id+"F0.wireOp",EDGE,"E12"),sQuery(id+"F0.wireOp",EDGE,"E13"),sQuery(id+"F0.wireOp",EDGE,"E14"),sQuery(id+"F0.wireOp",EDGE,"E15"),sQuery(id+"F0.wireOp",EDGE,"E18"),sQuery(id+"F0.wireOp",EDGE,"E19"),sQuery(id+"F0.wireOp",EDGE,"E20"),sQuery(id+"F0.wireOp",EDGE,"E21"),sQuery(id+"F0.wireOp",EDGE,"E22"),sQuery(id+"F0.wireOp",EDGE,"E25"),sQuery(id+"F0.wireOp",EDGE,"E26"),sQuery(id+"F0.wireOp",EDGE,"E27"),sQuery(id+"F0.wireOp",EDGE,"E28"),sQuery(id+"F0.wireOp",EDGE,"E29"),sQuery(id+"F0.wireOp",EDGE,"E30"),sQuery(id+"F0.wireOp",EDGE,"E31"),sQuery(id+"F0.wireOp",EDGE,"E32"),sQuery(id+"F0.wireOp",EDGE,"E33"),sQuery(id+"F0.wireOp",EDGE,"E34.0"),subQ1,subQ0,sQuery(id+"F0.wireOp",EDGE,"E34.3"),sQuery(id+"F0.wireOp",EDGE,"E34.4"),sQuery(id+"F0.wireOp",EDGE,"E34.5"),sQuery(id+"F0.wireOp",EDGE,"E34.6"),sQuery(id+"F0.wireOp",EDGE,"E34.7"),sQuery(id+"F0.wireOp",EDGE,"E34.8"),sQuery(id+"F0.wireOp",EDGE,"E34.9"),sQuery(id+"F0.wireOp",EDGE,"E34.10"),sQuery(id+"F0.wireOp",EDGE,"E34.11"),sQuery(id+"F0.wireOp",EDGE,"E34.12"),sQuery(id+"F0.wireOp",EDGE,"E34.13"),sQuery(id+"F0.wireOp",EDGE,"E34.14"),sQuery(id+"F0.wireOp",EDGE,"E34.15"),sQuery(id+"F0.wireOp",EDGE,"E34.16"),sQuery(id+"F0.wireOp",EDGE,"E34.17")])],"isStart":false})],"blendedInto":[makeQuery(id+"F1.opExtrude","CAP_FACE",FACE,{"disambiguationData":[OSD([sQuery(id+"F0.wireOp",EDGE,"E3"),sQuery(id+"F0.wireOp",EDGE,"E4"),sQuery(id+"F0.wireOp",EDGE,"E5"),sQuery(id+"F0.wireOp",EDGE,"E7"),sQuery(id+"F0.wireOp",EDGE,"E8"),sQuery(id+"F0.wireOp",EDGE,"E10"),sQuery(id+"F0.wireOp",EDGE,"E12"),sQuery(id+"F0.wireOp",EDGE,"E13"),sQuery(id+"F0.wireOp",EDGE,"E14"),sQuery(id+"F0.wireOp",EDGE,"E15"),sQuery(id+"F0.wireOp",EDGE,"E18"),sQuery(id+"F0.wireOp",EDGE,"E19"),sQuery(id+"F0.wireOp",EDGE,"E20"),sQuery(id+"F0.wireOp",EDGE,"E21"),sQuery(id+"F0.wireOp",EDGE,"E22"),sQuery(id+"F0.wireOp",EDGE,"E25"),sQuery(id+"F0.wireOp",EDGE,"E26"),sQuery(id+"F0.wireOp",EDGE,"E27"),sQuery(id+"F0.wireOp",EDGE,"E28"),sQuery(id+"F0.wireOp",EDGE,"E29"),sQuery(id+"F0.wireOp",EDGE,"E30"),sQuery(id+"F0.wireOp",EDGE,"E31"),sQuery(id+"F0.wireOp",EDGE,"E32"),sQuery(id+"F0.wireOp",EDGE,"E33"),sQuery(id+"F0.wireOp",EDGE,"E34.0"),subQ1,subQ0,sQuery(id+"F0.wireOp",EDGE,"E34.3"),sQuery(id+"F0.wireOp",EDGE,"E34.4"),sQuery(id+"F0.wireOp",EDGE,"E34.5"),sQuery(id+"F0.wireOp",EDGE,"E34.6"),sQuery(id+"F0.wireOp",EDGE,"E34.7"),sQuery(id+"F0.wireOp",EDGE,"E34.8"),sQuery(id+"F0.wireOp",EDGE,"E34.9"),sQuery(id+"F0.wireOp",EDGE,"E34.10"),sQuery(id+"F0.wireOp",EDGE,"E34.11"),sQuery(id+"F0.wireOp",EDGE,"E34.12"),sQuery(id+"F0.wireOp",EDGE,"E34.13"),sQuery(id+"F0.wireOp",EDGE,"E34.14"),sQuery(id+"F0.wireOp",EDGE,"E34.15"),sQuery(id+"F0.wireOp",EDGE,"E34.16"),sQuery(id+"F0.wireOp",EDGE,"E34.17")])],"isStart":false})]});}
            var Q26;
            Q26=makeQuery(id+"F1.opExtrude","CAP_EDGE",EDGE,{"disambiguationData":[OSD([sQuery(id+"F0.wireOp",EDGE,"E34.2")])],"isStart":false});
            var Q27;
            {var subQ0=sQuery(id+"F0.wireOp",EDGE,"E34.3");var subQ1=sQuery(id+"F0.wireOp",EDGE,"E34.2");Q27=makeQuery(id+"F3.opFillet","BLEND_EDGE",EDGE,{"blendedFrom":[makeQuery(id+"F1.opExtrude","SWEPT_EDGE",EDGE,{"disambiguationData":[OSD([subQ1,subQ0])]}),makeQuery(id+"F1.opExtrude","CAP_FACE",FACE,{"disambiguationData":[OSD([sQuery(id+"F0.wireOp",EDGE,"E3"),sQuery(id+"F0.wireOp",EDGE,"E4"),sQuery(id+"F0.wireOp",EDGE,"E5"),sQuery(id+"F0.wireOp",EDGE,"E7"),sQuery(id+"F0.wireOp",EDGE,"E8"),sQuery(id+"F0.wireOp",EDGE,"E10"),sQuery(id+"F0.wireOp",EDGE,"E12"),sQuery(id+"F0.wireOp",EDGE,"E13"),sQuery(id+"F0.wireOp",EDGE,"E14"),sQuery(id+"F0.wireOp",EDGE,"E15"),sQuery(id+"F0.wireOp",EDGE,"E18"),sQuery(id+"F0.wireOp",EDGE,"E19"),sQuery(id+"F0.wireOp",EDGE,"E20"),sQuery(id+"F0.wireOp",EDGE,"E21"),sQuery(id+"F0.wireOp",EDGE,"E22"),sQuery(id+"F0.wireOp",EDGE,"E25"),sQuery(id+"F0.wireOp",EDGE,"E26"),sQuery(id+"F0.wireOp",EDGE,"E27"),sQuery(id+"F0.wireOp",EDGE,"E28"),sQuery(id+"F0.wireOp",EDGE,"E29"),sQuery(id+"F0.wireOp",EDGE,"E30"),sQuery(id+"F0.wireOp",EDGE,"E31"),sQuery(id+"F0.wireOp",EDGE,"E32"),sQuery(id+"F0.wireOp",EDGE,"E33"),sQuery(id+"F0.wireOp",EDGE,"E34.0"),sQuery(id+"F0.wireOp",EDGE,"E34.1"),subQ1,subQ0,sQuery(id+"F0.wireOp",EDGE,"E34.4"),sQuery(id+"F0.wireOp",EDGE,"E34.5"),sQuery(id+"F0.wireOp",EDGE,"E34.6"),sQuery(id+"F0.wireOp",EDGE,"E34.7"),sQuery(id+"F0.wireOp",EDGE,"E34.8"),sQuery(id+"F0.wireOp",EDGE,"E34.9"),sQuery(id+"F0.wireOp",EDGE,"E34.10"),sQuery(id+"F0.wireOp",EDGE,"E34.11"),sQuery(id+"F0.wireOp",EDGE,"E34.12"),sQuery(id+"F0.wireOp",EDGE,"E34.13"),sQuery(id+"F0.wireOp",EDGE,"E34.14"),sQuery(id+"F0.wireOp",EDGE,"E34.15"),sQuery(id+"F0.wireOp",EDGE,"E34.16"),sQuery(id+"F0.wireOp",EDGE,"E34.17")])],"isStart":false})],"blendedInto":[makeQuery(id+"F1.opExtrude","CAP_FACE",FACE,{"disambiguationData":[OSD([sQuery(id+"F0.wireOp",EDGE,"E3"),sQuery(id+"F0.wireOp",EDGE,"E4"),sQuery(id+"F0.wireOp",EDGE,"E5"),sQuery(id+"F0.wireOp",EDGE,"E7"),sQuery(id+"F0.wireOp",EDGE,"E8"),sQuery(id+"F0.wireOp",EDGE,"E10"),sQuery(id+"F0.wireOp",EDGE,"E12"),sQuery(id+"F0.wireOp",EDGE,"E13"),sQuery(id+"F0.wireOp",EDGE,"E14"),sQuery(id+"F0.wireOp",EDGE,"E15"),sQuery(id+"F0.wireOp",EDGE,"E18"),sQuery(id+"F0.wireOp",EDGE,"E19"),sQuery(id+"F0.wireOp",EDGE,"E20"),sQuery(id+"F0.wireOp",EDGE,"E21"),sQuery(id+"F0.wireOp",EDGE,"E22"),sQuery(id+"F0.wireOp",EDGE,"E25"),sQuery(id+"F0.wireOp",EDGE,"E26"),sQuery(id+"F0.wireOp",EDGE,"E27"),sQuery(id+"F0.wireOp",EDGE,"E28"),sQuery(id+"F0.wireOp",EDGE,"E29"),sQuery(id+"F0.wireOp",EDGE,"E30"),sQuery(id+"F0.wireOp",EDGE,"E31"),sQuery(id+"F0.wireOp",EDGE,"E32"),sQuery(id+"F0.wireOp",EDGE,"E33"),sQuery(id+"F0.wireOp",EDGE,"E34.0"),sQuery(id+"F0.wireOp",EDGE,"E34.1"),subQ1,subQ0,sQuery(id+"F0.wireOp",EDGE,"E34.4"),sQuery(id+"F0.wireOp",EDGE,"E34.5"),sQuery(id+"F0.wireOp",EDGE,"E34.6"),sQuery(id+"F0.wireOp",EDGE,"E34.7"),sQuery(id+"F0.wireOp",EDGE,"E34.8"),sQuery(id+"F0.wireOp",EDGE,"E34.9"),sQuery(id+"F0.wireOp",EDGE,"E34.10"),sQuery(id+"F0.wireOp",EDGE,"E34.11"),sQuery(id+"F0.wireOp",EDGE,"E34.12"),sQuery(id+"F0.wireOp",EDGE,"E34.13"),sQuery(id+"F0.wireOp",EDGE,"E34.14"),sQuery(id+"F0.wireOp",EDGE,"E34.15"),sQuery(id+"F0.wireOp",EDGE,"E34.16"),sQuery(id+"F0.wireOp",EDGE,"E34.17")])],"isStart":false})]});}
            var Q28;
            Q28=makeQuery(id+"F1.opExtrude","CAP_EDGE",EDGE,{"disambiguationData":[OSD([sQuery(id+"F0.wireOp",EDGE,"E34.3")])],"isStart":false});
            var Q29;
            {var subQ0=sQuery(id+"F0.wireOp",EDGE,"E34.4");var subQ1=sQuery(id+"F0.wireOp",EDGE,"E34.3");Q29=makeQuery(id+"F2.opFillet","BLEND_EDGE",EDGE,{"blendedFrom":[makeQuery(id+"F1.opExtrude","SWEPT_EDGE",EDGE,{"disambiguationData":[OSD([subQ1,subQ0])]}),makeQuery(id+"F1.opExtrude","CAP_FACE",FACE,{"disambiguationData":[OSD([sQuery(id+"F0.wireOp",EDGE,"E3"),sQuery(id+"F0.wireOp",EDGE,"E4"),sQuery(id+"F0.wireOp",EDGE,"E5"),sQuery(id+"F0.wireOp",EDGE,"E7"),sQuery(id+"F0.wireOp",EDGE,"E8"),sQuery(id+"F0.wireOp",EDGE,"E10"),sQuery(id+"F0.wireOp",EDGE,"E12"),sQuery(id+"F0.wireOp",EDGE,"E13"),sQuery(id+"F0.wireOp",EDGE,"E14"),sQuery(id+"F0.wireOp",EDGE,"E15"),sQuery(id+"F0.wireOp",EDGE,"E18"),sQuery(id+"F0.wireOp",EDGE,"E19"),sQuery(id+"F0.wireOp",EDGE,"E20"),sQuery(id+"F0.wireOp",EDGE,"E21"),sQuery(id+"F0.wireOp",EDGE,"E22"),sQuery(id+"F0.wireOp",EDGE,"E25"),sQuery(id+"F0.wireOp",EDGE,"E26"),sQuery(id+"F0.wireOp",EDGE,"E27"),sQuery(id+"F0.wireOp",EDGE,"E28"),sQuery(id+"F0.wireOp",EDGE,"E29"),sQuery(id+"F0.wireOp",EDGE,"E30"),sQuery(id+"F0.wireOp",EDGE,"E31"),sQuery(id+"F0.wireOp",EDGE,"E32"),sQuery(id+"F0.wireOp",EDGE,"E33"),sQuery(id+"F0.wireOp",EDGE,"E34.0"),sQuery(id+"F0.wireOp",EDGE,"E34.1"),sQuery(id+"F0.wireOp",EDGE,"E34.2"),subQ1,subQ0,sQuery(id+"F0.wireOp",EDGE,"E34.5"),sQuery(id+"F0.wireOp",EDGE,"E34.6"),sQuery(id+"F0.wireOp",EDGE,"E34.7"),sQuery(id+"F0.wireOp",EDGE,"E34.8"),sQuery(id+"F0.wireOp",EDGE,"E34.9"),sQuery(id+"F0.wireOp",EDGE,"E34.10"),sQuery(id+"F0.wireOp",EDGE,"E34.11"),sQuery(id+"F0.wireOp",EDGE,"E34.12"),sQuery(id+"F0.wireOp",EDGE,"E34.13"),sQuery(id+"F0.wireOp",EDGE,"E34.14"),sQuery(id+"F0.wireOp",EDGE,"E34.15"),sQuery(id+"F0.wireOp",EDGE,"E34.16"),sQuery(id+"F0.wireOp",EDGE,"E34.17")])],"isStart":false})],"blendedInto":[makeQuery(id+"F1.opExtrude","CAP_FACE",FACE,{"disambiguationData":[OSD([sQuery(id+"F0.wireOp",EDGE,"E3"),sQuery(id+"F0.wireOp",EDGE,"E4"),sQuery(id+"F0.wireOp",EDGE,"E5"),sQuery(id+"F0.wireOp",EDGE,"E7"),sQuery(id+"F0.wireOp",EDGE,"E8"),sQuery(id+"F0.wireOp",EDGE,"E10"),sQuery(id+"F0.wireOp",EDGE,"E12"),sQuery(id+"F0.wireOp",EDGE,"E13"),sQuery(id+"F0.wireOp",EDGE,"E14"),sQuery(id+"F0.wireOp",EDGE,"E15"),sQuery(id+"F0.wireOp",EDGE,"E18"),sQuery(id+"F0.wireOp",EDGE,"E19"),sQuery(id+"F0.wireOp",EDGE,"E20"),sQuery(id+"F0.wireOp",EDGE,"E21"),sQuery(id+"F0.wireOp",EDGE,"E22"),sQuery(id+"F0.wireOp",EDGE,"E25"),sQuery(id+"F0.wireOp",EDGE,"E26"),sQuery(id+"F0.wireOp",EDGE,"E27"),sQuery(id+"F0.wireOp",EDGE,"E28"),sQuery(id+"F0.wireOp",EDGE,"E29"),sQuery(id+"F0.wireOp",EDGE,"E30"),sQuery(id+"F0.wireOp",EDGE,"E31"),sQuery(id+"F0.wireOp",EDGE,"E32"),sQuery(id+"F0.wireOp",EDGE,"E33"),sQuery(id+"F0.wireOp",EDGE,"E34.0"),sQuery(id+"F0.wireOp",EDGE,"E34.1"),sQuery(id+"F0.wireOp",EDGE,"E34.2"),subQ1,subQ0,sQuery(id+"F0.wireOp",EDGE,"E34.5"),sQuery(id+"F0.wireOp",EDGE,"E34.6"),sQuery(id+"F0.wireOp",EDGE,"E34.7"),sQuery(id+"F0.wireOp",EDGE,"E34.8"),sQuery(id+"F0.wireOp",EDGE,"E34.9"),sQuery(id+"F0.wireOp",EDGE,"E34.10"),sQuery(id+"F0.wireOp",EDGE,"E34.11"),sQuery(id+"F0.wireOp",EDGE,"E34.12"),sQuery(id+"F0.wireOp",EDGE,"E34.13"),sQuery(id+"F0.wireOp",EDGE,"E34.14"),sQuery(id+"F0.wireOp",EDGE,"E34.15"),sQuery(id+"F0.wireOp",EDGE,"E34.16"),sQuery(id+"F0.wireOp",EDGE,"E34.17")])],"isStart":false})]});}
            var Q30;
            Q30=makeQuery(id+"F1.opExtrude","CAP_EDGE",EDGE,{"disambiguationData":[OSD([sQuery(id+"F0.wireOp",EDGE,"E34.4")])],"isStart":false});
            var Q31;
            {var subQ0=sQuery(id+"F0.wireOp",EDGE,"E34.6");var subQ1=sQuery(id+"F0.wireOp",EDGE,"E34.4");Q31=makeQuery(id+"F2.opFillet","BLEND_EDGE",EDGE,{"blendedFrom":[makeQuery(id+"F1.opExtrude","SWEPT_EDGE",EDGE,{"disambiguationData":[OSD([subQ1,subQ0])]}),makeQuery(id+"F1.opExtrude","CAP_FACE",FACE,{"disambiguationData":[OSD([sQuery(id+"F0.wireOp",EDGE,"E3"),sQuery(id+"F0.wireOp",EDGE,"E4"),sQuery(id+"F0.wireOp",EDGE,"E5"),sQuery(id+"F0.wireOp",EDGE,"E7"),sQuery(id+"F0.wireOp",EDGE,"E8"),sQuery(id+"F0.wireOp",EDGE,"E10"),sQuery(id+"F0.wireOp",EDGE,"E12"),sQuery(id+"F0.wireOp",EDGE,"E13"),sQuery(id+"F0.wireOp",EDGE,"E14"),sQuery(id+"F0.wireOp",EDGE,"E15"),sQuery(id+"F0.wireOp",EDGE,"E18"),sQuery(id+"F0.wireOp",EDGE,"E19"),sQuery(id+"F0.wireOp",EDGE,"E20"),sQuery(id+"F0.wireOp",EDGE,"E21"),sQuery(id+"F0.wireOp",EDGE,"E22"),sQuery(id+"F0.wireOp",EDGE,"E25"),sQuery(id+"F0.wireOp",EDGE,"E26"),sQuery(id+"F0.wireOp",EDGE,"E27"),sQuery(id+"F0.wireOp",EDGE,"E28"),sQuery(id+"F0.wireOp",EDGE,"E29"),sQuery(id+"F0.wireOp",EDGE,"E30"),sQuery(id+"F0.wireOp",EDGE,"E31"),sQuery(id+"F0.wireOp",EDGE,"E32"),sQuery(id+"F0.wireOp",EDGE,"E33"),sQuery(id+"F0.wireOp",EDGE,"E34.0"),sQuery(id+"F0.wireOp",EDGE,"E34.1"),sQuery(id+"F0.wireOp",EDGE,"E34.2"),sQuery(id+"F0.wireOp",EDGE,"E34.3"),subQ1,sQuery(id+"F0.wireOp",EDGE,"E34.5"),subQ0,sQuery(id+"F0.wireOp",EDGE,"E34.7"),sQuery(id+"F0.wireOp",EDGE,"E34.8"),sQuery(id+"F0.wireOp",EDGE,"E34.9"),sQuery(id+"F0.wireOp",EDGE,"E34.10"),sQuery(id+"F0.wireOp",EDGE,"E34.11"),sQuery(id+"F0.wireOp",EDGE,"E34.12"),sQuery(id+"F0.wireOp",EDGE,"E34.13"),sQuery(id+"F0.wireOp",EDGE,"E34.14"),sQuery(id+"F0.wireOp",EDGE,"E34.15"),sQuery(id+"F0.wireOp",EDGE,"E34.16"),sQuery(id+"F0.wireOp",EDGE,"E34.17")])],"isStart":false})],"blendedInto":[makeQuery(id+"F1.opExtrude","CAP_FACE",FACE,{"disambiguationData":[OSD([sQuery(id+"F0.wireOp",EDGE,"E3"),sQuery(id+"F0.wireOp",EDGE,"E4"),sQuery(id+"F0.wireOp",EDGE,"E5"),sQuery(id+"F0.wireOp",EDGE,"E7"),sQuery(id+"F0.wireOp",EDGE,"E8"),sQuery(id+"F0.wireOp",EDGE,"E10"),sQuery(id+"F0.wireOp",EDGE,"E12"),sQuery(id+"F0.wireOp",EDGE,"E13"),sQuery(id+"F0.wireOp",EDGE,"E14"),sQuery(id+"F0.wireOp",EDGE,"E15"),sQuery(id+"F0.wireOp",EDGE,"E18"),sQuery(id+"F0.wireOp",EDGE,"E19"),sQuery(id+"F0.wireOp",EDGE,"E20"),sQuery(id+"F0.wireOp",EDGE,"E21"),sQuery(id+"F0.wireOp",EDGE,"E22"),sQuery(id+"F0.wireOp",EDGE,"E25"),sQuery(id+"F0.wireOp",EDGE,"E26"),sQuery(id+"F0.wireOp",EDGE,"E27"),sQuery(id+"F0.wireOp",EDGE,"E28"),sQuery(id+"F0.wireOp",EDGE,"E29"),sQuery(id+"F0.wireOp",EDGE,"E30"),sQuery(id+"F0.wireOp",EDGE,"E31"),sQuery(id+"F0.wireOp",EDGE,"E32"),sQuery(id+"F0.wireOp",EDGE,"E33"),sQuery(id+"F0.wireOp",EDGE,"E34.0"),sQuery(id+"F0.wireOp",EDGE,"E34.1"),sQuery(id+"F0.wireOp",EDGE,"E34.2"),sQuery(id+"F0.wireOp",EDGE,"E34.3"),subQ1,sQuery(id+"F0.wireOp",EDGE,"E34.5"),subQ0,sQuery(id+"F0.wireOp",EDGE,"E34.7"),sQuery(id+"F0.wireOp",EDGE,"E34.8"),sQuery(id+"F0.wireOp",EDGE,"E34.9"),sQuery(id+"F0.wireOp",EDGE,"E34.10"),sQuery(id+"F0.wireOp",EDGE,"E34.11"),sQuery(id+"F0.wireOp",EDGE,"E34.12"),sQuery(id+"F0.wireOp",EDGE,"E34.13"),sQuery(id+"F0.wireOp",EDGE,"E34.14"),sQuery(id+"F0.wireOp",EDGE,"E34.15"),sQuery(id+"F0.wireOp",EDGE,"E34.16"),sQuery(id+"F0.wireOp",EDGE,"E34.17")])],"isStart":false})]});}
            var Q32;
            Q32=makeQuery(id+"F1.opExtrude","CAP_EDGE",EDGE,{"disambiguationData":[OSD([sQuery(id+"F0.wireOp",EDGE,"E34.6")])],"isStart":false});
            var Q33;
            {var subQ0=sQuery(id+"F0.wireOp",EDGE,"E34.7");var subQ1=sQuery(id+"F0.wireOp",EDGE,"E34.6");Q33=makeQuery(id+"F3.opFillet","BLEND_EDGE",EDGE,{"blendedFrom":[makeQuery(id+"F1.opExtrude","SWEPT_EDGE",EDGE,{"disambiguationData":[OSD([subQ1,subQ0])]}),makeQuery(id+"F1.opExtrude","CAP_FACE",FACE,{"disambiguationData":[OSD([sQuery(id+"F0.wireOp",EDGE,"E3"),sQuery(id+"F0.wireOp",EDGE,"E4"),sQuery(id+"F0.wireOp",EDGE,"E5"),sQuery(id+"F0.wireOp",EDGE,"E7"),sQuery(id+"F0.wireOp",EDGE,"E8"),sQuery(id+"F0.wireOp",EDGE,"E10"),sQuery(id+"F0.wireOp",EDGE,"E12"),sQuery(id+"F0.wireOp",EDGE,"E13"),sQuery(id+"F0.wireOp",EDGE,"E14"),sQuery(id+"F0.wireOp",EDGE,"E15"),sQuery(id+"F0.wireOp",EDGE,"E18"),sQuery(id+"F0.wireOp",EDGE,"E19"),sQuery(id+"F0.wireOp",EDGE,"E20"),sQuery(id+"F0.wireOp",EDGE,"E21"),sQuery(id+"F0.wireOp",EDGE,"E22"),sQuery(id+"F0.wireOp",EDGE,"E25"),sQuery(id+"F0.wireOp",EDGE,"E26"),sQuery(id+"F0.wireOp",EDGE,"E27"),sQuery(id+"F0.wireOp",EDGE,"E28"),sQuery(id+"F0.wireOp",EDGE,"E29"),sQuery(id+"F0.wireOp",EDGE,"E30"),sQuery(id+"F0.wireOp",EDGE,"E31"),sQuery(id+"F0.wireOp",EDGE,"E32"),sQuery(id+"F0.wireOp",EDGE,"E33"),sQuery(id+"F0.wireOp",EDGE,"E34.0"),sQuery(id+"F0.wireOp",EDGE,"E34.1"),sQuery(id+"F0.wireOp",EDGE,"E34.2"),sQuery(id+"F0.wireOp",EDGE,"E34.3"),sQuery(id+"F0.wireOp",EDGE,"E34.4"),sQuery(id+"F0.wireOp",EDGE,"E34.5"),subQ1,subQ0,sQuery(id+"F0.wireOp",EDGE,"E34.8"),sQuery(id+"F0.wireOp",EDGE,"E34.9"),sQuery(id+"F0.wireOp",EDGE,"E34.10"),sQuery(id+"F0.wireOp",EDGE,"E34.11"),sQuery(id+"F0.wireOp",EDGE,"E34.12"),sQuery(id+"F0.wireOp",EDGE,"E34.13"),sQuery(id+"F0.wireOp",EDGE,"E34.14"),sQuery(id+"F0.wireOp",EDGE,"E34.15"),sQuery(id+"F0.wireOp",EDGE,"E34.16"),sQuery(id+"F0.wireOp",EDGE,"E34.17")])],"isStart":false})],"blendedInto":[makeQuery(id+"F1.opExtrude","CAP_FACE",FACE,{"disambiguationData":[OSD([sQuery(id+"F0.wireOp",EDGE,"E3"),sQuery(id+"F0.wireOp",EDGE,"E4"),sQuery(id+"F0.wireOp",EDGE,"E5"),sQuery(id+"F0.wireOp",EDGE,"E7"),sQuery(id+"F0.wireOp",EDGE,"E8"),sQuery(id+"F0.wireOp",EDGE,"E10"),sQuery(id+"F0.wireOp",EDGE,"E12"),sQuery(id+"F0.wireOp",EDGE,"E13"),sQuery(id+"F0.wireOp",EDGE,"E14"),sQuery(id+"F0.wireOp",EDGE,"E15"),sQuery(id+"F0.wireOp",EDGE,"E18"),sQuery(id+"F0.wireOp",EDGE,"E19"),sQuery(id+"F0.wireOp",EDGE,"E20"),sQuery(id+"F0.wireOp",EDGE,"E21"),sQuery(id+"F0.wireOp",EDGE,"E22"),sQuery(id+"F0.wireOp",EDGE,"E25"),sQuery(id+"F0.wireOp",EDGE,"E26"),sQuery(id+"F0.wireOp",EDGE,"E27"),sQuery(id+"F0.wireOp",EDGE,"E28"),sQuery(id+"F0.wireOp",EDGE,"E29"),sQuery(id+"F0.wireOp",EDGE,"E30"),sQuery(id+"F0.wireOp",EDGE,"E31"),sQuery(id+"F0.wireOp",EDGE,"E32"),sQuery(id+"F0.wireOp",EDGE,"E33"),sQuery(id+"F0.wireOp",EDGE,"E34.0"),sQuery(id+"F0.wireOp",EDGE,"E34.1"),sQuery(id+"F0.wireOp",EDGE,"E34.2"),sQuery(id+"F0.wireOp",EDGE,"E34.3"),sQuery(id+"F0.wireOp",EDGE,"E34.4"),sQuery(id+"F0.wireOp",EDGE,"E34.5"),subQ1,subQ0,sQuery(id+"F0.wireOp",EDGE,"E34.8"),sQuery(id+"F0.wireOp",EDGE,"E34.9"),sQuery(id+"F0.wireOp",EDGE,"E34.10"),sQuery(id+"F0.wireOp",EDGE,"E34.11"),sQuery(id+"F0.wireOp",EDGE,"E34.12"),sQuery(id+"F0.wireOp",EDGE,"E34.13"),sQuery(id+"F0.wireOp",EDGE,"E34.14"),sQuery(id+"F0.wireOp",EDGE,"E34.15"),sQuery(id+"F0.wireOp",EDGE,"E34.16"),sQuery(id+"F0.wireOp",EDGE,"E34.17")])],"isStart":false})]});}
            var Q34;
            Q34=makeQuery(id+"F1.opExtrude","CAP_EDGE",EDGE,{"disambiguationData":[OSD([sQuery(id+"F0.wireOp",EDGE,"E34.7")])],"isStart":false});
            var Q35;
            {var subQ0=sQuery(id+"F0.wireOp",EDGE,"E34.17");var subQ1=sQuery(id+"F0.wireOp",EDGE,"E34.7");Q35=makeQuery(id+"F3.opFillet","BLEND_EDGE",EDGE,{"blendedFrom":[makeQuery(id+"F1.opExtrude","SWEPT_EDGE",EDGE,{"disambiguationData":[OSD([subQ1,subQ0])]}),makeQuery(id+"F1.opExtrude","CAP_FACE",FACE,{"disambiguationData":[OSD([sQuery(id+"F0.wireOp",EDGE,"E3"),sQuery(id+"F0.wireOp",EDGE,"E4"),sQuery(id+"F0.wireOp",EDGE,"E5"),sQuery(id+"F0.wireOp",EDGE,"E7"),sQuery(id+"F0.wireOp",EDGE,"E8"),sQuery(id+"F0.wireOp",EDGE,"E10"),sQuery(id+"F0.wireOp",EDGE,"E12"),sQuery(id+"F0.wireOp",EDGE,"E13"),sQuery(id+"F0.wireOp",EDGE,"E14"),sQuery(id+"F0.wireOp",EDGE,"E15"),sQuery(id+"F0.wireOp",EDGE,"E18"),sQuery(id+"F0.wireOp",EDGE,"E19"),sQuery(id+"F0.wireOp",EDGE,"E20"),sQuery(id+"F0.wireOp",EDGE,"E21"),sQuery(id+"F0.wireOp",EDGE,"E22"),sQuery(id+"F0.wireOp",EDGE,"E25"),sQuery(id+"F0.wireOp",EDGE,"E26"),sQuery(id+"F0.wireOp",EDGE,"E27"),sQuery(id+"F0.wireOp",EDGE,"E28"),sQuery(id+"F0.wireOp",EDGE,"E29"),sQuery(id+"F0.wireOp",EDGE,"E30"),sQuery(id+"F0.wireOp",EDGE,"E31"),sQuery(id+"F0.wireOp",EDGE,"E32"),sQuery(id+"F0.wireOp",EDGE,"E33"),sQuery(id+"F0.wireOp",EDGE,"E34.0"),sQuery(id+"F0.wireOp",EDGE,"E34.1"),sQuery(id+"F0.wireOp",EDGE,"E34.2"),sQuery(id+"F0.wireOp",EDGE,"E34.3"),sQuery(id+"F0.wireOp",EDGE,"E34.4"),sQuery(id+"F0.wireOp",EDGE,"E34.5"),sQuery(id+"F0.wireOp",EDGE,"E34.6"),subQ1,sQuery(id+"F0.wireOp",EDGE,"E34.8"),sQuery(id+"F0.wireOp",EDGE,"E34.9"),sQuery(id+"F0.wireOp",EDGE,"E34.10"),sQuery(id+"F0.wireOp",EDGE,"E34.11"),sQuery(id+"F0.wireOp",EDGE,"E34.12"),sQuery(id+"F0.wireOp",EDGE,"E34.13"),sQuery(id+"F0.wireOp",EDGE,"E34.14"),sQuery(id+"F0.wireOp",EDGE,"E34.15"),sQuery(id+"F0.wireOp",EDGE,"E34.16"),subQ0])],"isStart":false})],"blendedInto":[makeQuery(id+"F1.opExtrude","CAP_FACE",FACE,{"disambiguationData":[OSD([sQuery(id+"F0.wireOp",EDGE,"E3"),sQuery(id+"F0.wireOp",EDGE,"E4"),sQuery(id+"F0.wireOp",EDGE,"E5"),sQuery(id+"F0.wireOp",EDGE,"E7"),sQuery(id+"F0.wireOp",EDGE,"E8"),sQuery(id+"F0.wireOp",EDGE,"E10"),sQuery(id+"F0.wireOp",EDGE,"E12"),sQuery(id+"F0.wireOp",EDGE,"E13"),sQuery(id+"F0.wireOp",EDGE,"E14"),sQuery(id+"F0.wireOp",EDGE,"E15"),sQuery(id+"F0.wireOp",EDGE,"E18"),sQuery(id+"F0.wireOp",EDGE,"E19"),sQuery(id+"F0.wireOp",EDGE,"E20"),sQuery(id+"F0.wireOp",EDGE,"E21"),sQuery(id+"F0.wireOp",EDGE,"E22"),sQuery(id+"F0.wireOp",EDGE,"E25"),sQuery(id+"F0.wireOp",EDGE,"E26"),sQuery(id+"F0.wireOp",EDGE,"E27"),sQuery(id+"F0.wireOp",EDGE,"E28"),sQuery(id+"F0.wireOp",EDGE,"E29"),sQuery(id+"F0.wireOp",EDGE,"E30"),sQuery(id+"F0.wireOp",EDGE,"E31"),sQuery(id+"F0.wireOp",EDGE,"E32"),sQuery(id+"F0.wireOp",EDGE,"E33"),sQuery(id+"F0.wireOp",EDGE,"E34.0"),sQuery(id+"F0.wireOp",EDGE,"E34.1"),sQuery(id+"F0.wireOp",EDGE,"E34.2"),sQuery(id+"F0.wireOp",EDGE,"E34.3"),sQuery(id+"F0.wireOp",EDGE,"E34.4"),sQuery(id+"F0.wireOp",EDGE,"E34.5"),sQuery(id+"F0.wireOp",EDGE,"E34.6"),subQ1,sQuery(id+"F0.wireOp",EDGE,"E34.8"),sQuery(id+"F0.wireOp",EDGE,"E34.9"),sQuery(id+"F0.wireOp",EDGE,"E34.10"),sQuery(id+"F0.wireOp",EDGE,"E34.11"),sQuery(id+"F0.wireOp",EDGE,"E34.12"),sQuery(id+"F0.wireOp",EDGE,"E34.13"),sQuery(id+"F0.wireOp",EDGE,"E34.14"),sQuery(id+"F0.wireOp",EDGE,"E34.15"),sQuery(id+"F0.wireOp",EDGE,"E34.16"),subQ0])],"isStart":false})]});}
            var Q36;
            Q36=makeQuery(id+"F1.opExtrude","CAP_EDGE",EDGE,{"disambiguationData":[OSD([sQuery(id+"F0.wireOp",EDGE,"E34.9")])],"isStart":true});
            var Q37;
            {var subQ0=sQuery(id+"F0.wireOp",EDGE,"E34.9");var subQ1=sQuery(id+"F0.wireOp",EDGE,"E34.8");Q37=makeQuery(id+"F3.opFillet","BLEND_EDGE",EDGE,{"blendedFrom":[makeQuery(id+"F1.opExtrude","SWEPT_EDGE",EDGE,{"disambiguationData":[OSD([subQ1,subQ0])]}),makeQuery(id+"F1.opExtrude","CAP_FACE",FACE,{"disambiguationData":[OSD([sQuery(id+"F0.wireOp",EDGE,"E3"),sQuery(id+"F0.wireOp",EDGE,"E4"),sQuery(id+"F0.wireOp",EDGE,"E5"),sQuery(id+"F0.wireOp",EDGE,"E7"),sQuery(id+"F0.wireOp",EDGE,"E8"),sQuery(id+"F0.wireOp",EDGE,"E10"),sQuery(id+"F0.wireOp",EDGE,"E12"),sQuery(id+"F0.wireOp",EDGE,"E13"),sQuery(id+"F0.wireOp",EDGE,"E14"),sQuery(id+"F0.wireOp",EDGE,"E15"),sQuery(id+"F0.wireOp",EDGE,"E18"),sQuery(id+"F0.wireOp",EDGE,"E19"),sQuery(id+"F0.wireOp",EDGE,"E20"),sQuery(id+"F0.wireOp",EDGE,"E21"),sQuery(id+"F0.wireOp",EDGE,"E22"),sQuery(id+"F0.wireOp",EDGE,"E25"),sQuery(id+"F0.wireOp",EDGE,"E26"),sQuery(id+"F0.wireOp",EDGE,"E27"),sQuery(id+"F0.wireOp",EDGE,"E28"),sQuery(id+"F0.wireOp",EDGE,"E29"),sQuery(id+"F0.wireOp",EDGE,"E30"),sQuery(id+"F0.wireOp",EDGE,"E31"),sQuery(id+"F0.wireOp",EDGE,"E32"),sQuery(id+"F0.wireOp",EDGE,"E33"),sQuery(id+"F0.wireOp",EDGE,"E34.0"),sQuery(id+"F0.wireOp",EDGE,"E34.1"),sQuery(id+"F0.wireOp",EDGE,"E34.2"),sQuery(id+"F0.wireOp",EDGE,"E34.3"),sQuery(id+"F0.wireOp",EDGE,"E34.4"),sQuery(id+"F0.wireOp",EDGE,"E34.5"),sQuery(id+"F0.wireOp",EDGE,"E34.6"),sQuery(id+"F0.wireOp",EDGE,"E34.7"),subQ1,subQ0,sQuery(id+"F0.wireOp",EDGE,"E34.10"),sQuery(id+"F0.wireOp",EDGE,"E34.11"),sQuery(id+"F0.wireOp",EDGE,"E34.12"),sQuery(id+"F0.wireOp",EDGE,"E34.13"),sQuery(id+"F0.wireOp",EDGE,"E34.14"),sQuery(id+"F0.wireOp",EDGE,"E34.15"),sQuery(id+"F0.wireOp",EDGE,"E34.16"),sQuery(id+"F0.wireOp",EDGE,"E34.17")])],"isStart":true})],"blendedInto":[makeQuery(id+"F1.opExtrude","CAP_FACE",FACE,{"disambiguationData":[OSD([sQuery(id+"F0.wireOp",EDGE,"E3"),sQuery(id+"F0.wireOp",EDGE,"E4"),sQuery(id+"F0.wireOp",EDGE,"E5"),sQuery(id+"F0.wireOp",EDGE,"E7"),sQuery(id+"F0.wireOp",EDGE,"E8"),sQuery(id+"F0.wireOp",EDGE,"E10"),sQuery(id+"F0.wireOp",EDGE,"E12"),sQuery(id+"F0.wireOp",EDGE,"E13"),sQuery(id+"F0.wireOp",EDGE,"E14"),sQuery(id+"F0.wireOp",EDGE,"E15"),sQuery(id+"F0.wireOp",EDGE,"E18"),sQuery(id+"F0.wireOp",EDGE,"E19"),sQuery(id+"F0.wireOp",EDGE,"E20"),sQuery(id+"F0.wireOp",EDGE,"E21"),sQuery(id+"F0.wireOp",EDGE,"E22"),sQuery(id+"F0.wireOp",EDGE,"E25"),sQuery(id+"F0.wireOp",EDGE,"E26"),sQuery(id+"F0.wireOp",EDGE,"E27"),sQuery(id+"F0.wireOp",EDGE,"E28"),sQuery(id+"F0.wireOp",EDGE,"E29"),sQuery(id+"F0.wireOp",EDGE,"E30"),sQuery(id+"F0.wireOp",EDGE,"E31"),sQuery(id+"F0.wireOp",EDGE,"E32"),sQuery(id+"F0.wireOp",EDGE,"E33"),sQuery(id+"F0.wireOp",EDGE,"E34.0"),sQuery(id+"F0.wireOp",EDGE,"E34.1"),sQuery(id+"F0.wireOp",EDGE,"E34.2"),sQuery(id+"F0.wireOp",EDGE,"E34.3"),sQuery(id+"F0.wireOp",EDGE,"E34.4"),sQuery(id+"F0.wireOp",EDGE,"E34.5"),sQuery(id+"F0.wireOp",EDGE,"E34.6"),sQuery(id+"F0.wireOp",EDGE,"E34.7"),subQ1,subQ0,sQuery(id+"F0.wireOp",EDGE,"E34.10"),sQuery(id+"F0.wireOp",EDGE,"E34.11"),sQuery(id+"F0.wireOp",EDGE,"E34.12"),sQuery(id+"F0.wireOp",EDGE,"E34.13"),sQuery(id+"F0.wireOp",EDGE,"E34.14"),sQuery(id+"F0.wireOp",EDGE,"E34.15"),sQuery(id+"F0.wireOp",EDGE,"E34.16"),sQuery(id+"F0.wireOp",EDGE,"E34.17")])],"isStart":true})]});}
            var Q38;
            Q38=makeQuery(id+"F1.opExtrude","CAP_EDGE",EDGE,{"disambiguationData":[OSD([sQuery(id+"F0.wireOp",EDGE,"E34.8")])],"isStart":true});
            var Q39;
            {var subQ0=sQuery(id+"F0.wireOp",EDGE,"E34.12");var subQ1=sQuery(id+"F0.wireOp",EDGE,"E34.8");Q39=makeQuery(id+"F3.opFillet","BLEND_EDGE",EDGE,{"blendedFrom":[makeQuery(id+"F1.opExtrude","SWEPT_EDGE",EDGE,{"disambiguationData":[OSD([subQ1,subQ0])]}),makeQuery(id+"F1.opExtrude","CAP_FACE",FACE,{"disambiguationData":[OSD([sQuery(id+"F0.wireOp",EDGE,"E3"),sQuery(id+"F0.wireOp",EDGE,"E4"),sQuery(id+"F0.wireOp",EDGE,"E5"),sQuery(id+"F0.wireOp",EDGE,"E7"),sQuery(id+"F0.wireOp",EDGE,"E8"),sQuery(id+"F0.wireOp",EDGE,"E10"),sQuery(id+"F0.wireOp",EDGE,"E12"),sQuery(id+"F0.wireOp",EDGE,"E13"),sQuery(id+"F0.wireOp",EDGE,"E14"),sQuery(id+"F0.wireOp",EDGE,"E15"),sQuery(id+"F0.wireOp",EDGE,"E18"),sQuery(id+"F0.wireOp",EDGE,"E19"),sQuery(id+"F0.wireOp",EDGE,"E20"),sQuery(id+"F0.wireOp",EDGE,"E21"),sQuery(id+"F0.wireOp",EDGE,"E22"),sQuery(id+"F0.wireOp",EDGE,"E25"),sQuery(id+"F0.wireOp",EDGE,"E26"),sQuery(id+"F0.wireOp",EDGE,"E27"),sQuery(id+"F0.wireOp",EDGE,"E28"),sQuery(id+"F0.wireOp",EDGE,"E29"),sQuery(id+"F0.wireOp",EDGE,"E30"),sQuery(id+"F0.wireOp",EDGE,"E31"),sQuery(id+"F0.wireOp",EDGE,"E32"),sQuery(id+"F0.wireOp",EDGE,"E33"),sQuery(id+"F0.wireOp",EDGE,"E34.0"),sQuery(id+"F0.wireOp",EDGE,"E34.1"),sQuery(id+"F0.wireOp",EDGE,"E34.2"),sQuery(id+"F0.wireOp",EDGE,"E34.3"),sQuery(id+"F0.wireOp",EDGE,"E34.4"),sQuery(id+"F0.wireOp",EDGE,"E34.5"),sQuery(id+"F0.wireOp",EDGE,"E34.6"),sQuery(id+"F0.wireOp",EDGE,"E34.7"),subQ1,sQuery(id+"F0.wireOp",EDGE,"E34.9"),sQuery(id+"F0.wireOp",EDGE,"E34.10"),sQuery(id+"F0.wireOp",EDGE,"E34.11"),subQ0,sQuery(id+"F0.wireOp",EDGE,"E34.13"),sQuery(id+"F0.wireOp",EDGE,"E34.14"),sQuery(id+"F0.wireOp",EDGE,"E34.15"),sQuery(id+"F0.wireOp",EDGE,"E34.16"),sQuery(id+"F0.wireOp",EDGE,"E34.17")])],"isStart":true})],"blendedInto":[makeQuery(id+"F1.opExtrude","CAP_FACE",FACE,{"disambiguationData":[OSD([sQuery(id+"F0.wireOp",EDGE,"E3"),sQuery(id+"F0.wireOp",EDGE,"E4"),sQuery(id+"F0.wireOp",EDGE,"E5"),sQuery(id+"F0.wireOp",EDGE,"E7"),sQuery(id+"F0.wireOp",EDGE,"E8"),sQuery(id+"F0.wireOp",EDGE,"E10"),sQuery(id+"F0.wireOp",EDGE,"E12"),sQuery(id+"F0.wireOp",EDGE,"E13"),sQuery(id+"F0.wireOp",EDGE,"E14"),sQuery(id+"F0.wireOp",EDGE,"E15"),sQuery(id+"F0.wireOp",EDGE,"E18"),sQuery(id+"F0.wireOp",EDGE,"E19"),sQuery(id+"F0.wireOp",EDGE,"E20"),sQuery(id+"F0.wireOp",EDGE,"E21"),sQuery(id+"F0.wireOp",EDGE,"E22"),sQuery(id+"F0.wireOp",EDGE,"E25"),sQuery(id+"F0.wireOp",EDGE,"E26"),sQuery(id+"F0.wireOp",EDGE,"E27"),sQuery(id+"F0.wireOp",EDGE,"E28"),sQuery(id+"F0.wireOp",EDGE,"E29"),sQuery(id+"F0.wireOp",EDGE,"E30"),sQuery(id+"F0.wireOp",EDGE,"E31"),sQuery(id+"F0.wireOp",EDGE,"E32"),sQuery(id+"F0.wireOp",EDGE,"E33"),sQuery(id+"F0.wireOp",EDGE,"E34.0"),sQuery(id+"F0.wireOp",EDGE,"E34.1"),sQuery(id+"F0.wireOp",EDGE,"E34.2"),sQuery(id+"F0.wireOp",EDGE,"E34.3"),sQuery(id+"F0.wireOp",EDGE,"E34.4"),sQuery(id+"F0.wireOp",EDGE,"E34.5"),sQuery(id+"F0.wireOp",EDGE,"E34.6"),sQuery(id+"F0.wireOp",EDGE,"E34.7"),subQ1,sQuery(id+"F0.wireOp",EDGE,"E34.9"),sQuery(id+"F0.wireOp",EDGE,"E34.10"),sQuery(id+"F0.wireOp",EDGE,"E34.11"),subQ0,sQuery(id+"F0.wireOp",EDGE,"E34.13"),sQuery(id+"F0.wireOp",EDGE,"E34.14"),sQuery(id+"F0.wireOp",EDGE,"E34.15"),sQuery(id+"F0.wireOp",EDGE,"E34.16"),sQuery(id+"F0.wireOp",EDGE,"E34.17")])],"isStart":true})]});}
            fillet(context, id + "F4", {"entities" : qUnion([Q0, Q1, Q2, Q3, Q4, Q5, Q6, Q7, Q8, Q9, Q10, Q11, Q12, Q13, Q14, Q15, Q16, Q17, Q18, Q19, Q20, Q21, Q22, Q23, Q24, Q25, Q26, Q27, Q28, Q29, Q30, Q31, Q32, Q33, Q34, Q35, Q36, Q37, Q38, Q39]), "radius" : 1 * mm, "tangentPropagation" : true, "allowEdgeOverflow" : false});
        }
        {
            var Q0;
            Q0=makeQuery(id+"F0.imprint","IMPRINT",FACE,{"disambiguationData":[TD([[makeQuery(id+"F0.imprint","IMPRINT",EDGE,{"derivedFrom":sQuery(id+"F0.wireOp",EDGE,"E3")}),-1.0]])]});
            extrude(context, id + "F5", {"entities" : qUnion([Q0]), "oppositeDirection" : true, "depth" : 2 * mm, "offsetDistance" : 25 * mm});
        }
        {
            var Q0;
            Q0=makeQuery(id+"F5.opExtrude","CAP_FACE",FACE,{"disambiguationData":[OSD([sQuery(id+"F0.wireOp",EDGE,"E3"),sQuery(id+"F0.wireOp",EDGE,"E4"),sQuery(id+"F0.wireOp",EDGE,"E5"),sQuery(id+"F0.wireOp",EDGE,"E7"),sQuery(id+"F0.wireOp",EDGE,"E8"),sQuery(id+"F0.wireOp",EDGE,"E10"),sQuery(id+"F0.wireOp",EDGE,"E12"),sQuery(id+"F0.wireOp",EDGE,"E13"),sQuery(id+"F0.wireOp",EDGE,"E14"),sQuery(id+"F0.wireOp",EDGE,"E15"),sQuery(id+"F0.wireOp",EDGE,"E18"),sQuery(id+"F0.wireOp",EDGE,"E19"),sQuery(id+"F0.wireOp",EDGE,"E20"),sQuery(id+"F0.wireOp",EDGE,"E21"),sQuery(id+"F0.wireOp",EDGE,"E22"),sQuery(id+"F0.wireOp",EDGE,"E25"),sQuery(id+"F0.wireOp",EDGE,"E26"),sQuery(id+"F0.wireOp",EDGE,"E27"),sQuery(id+"F0.wireOp",EDGE,"E28"),sQuery(id+"F0.wireOp",EDGE,"E29"),sQuery(id+"F0.wireOp",EDGE,"E30"),sQuery(id+"F0.wireOp",EDGE,"E31"),sQuery(id+"F0.wireOp",EDGE,"E32"),sQuery(id+"F0.wireOp",EDGE,"E33")])],"isStart":false});
            fillet(context, id + "F6", {"entities" : qUnion([Q0]), "radius" : 2 * mm, "tangentPropagation" : true, "allowEdgeOverflow" : false});
        }
    });
